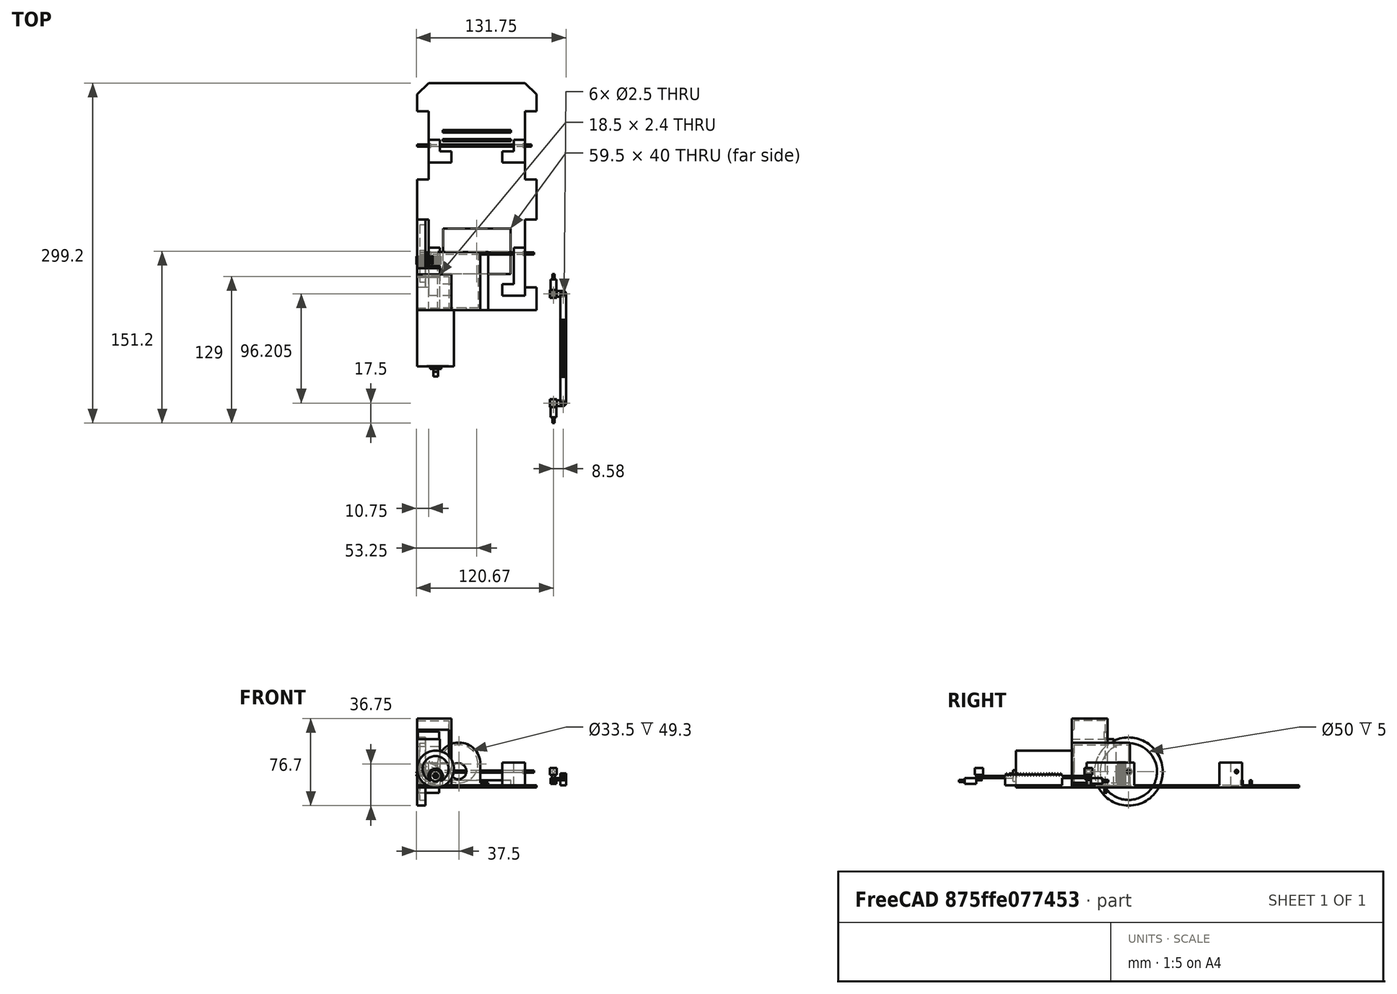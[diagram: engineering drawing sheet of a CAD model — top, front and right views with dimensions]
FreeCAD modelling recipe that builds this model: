
FCSTD DOCUMENT  (FreeCAD 0.21R33668 +26 (Git))
Label: spy_car_model
License: All rights reserved
LicenseURL: http://en.wikipedia.org/wiki/All_rights_reserved
objects: Sketcher::SketchObject×57, PartDesign::Pad×40, PartDesign::Pocket×18, PartDesign::Body×15, App::Part×9, PartDesign::Fillet×5, Part::Part2DObjectPython×3, Mesh::Feature×2, Spreadsheet::Sheet×1, PartDesign::FeaturePython×1
note: 202 computed .brp shape members not serialized (recipe doc carries the construction recipe); baked Part::Feature solids carry a one-line shape summary decoded from their .brp

FEATURE [Spreadsheet::Sheet] Spreadsheet
  cells = A1='12vdc gear motor; D1='servo ; G1='Car body; J1='rods; M1='motor holder; P1='turning mechanism; S1='wheels; A2='diameter; B2(dcm_diam)==32.5 mm; D2='total length; E2(serv_len)==45 mm; G2='height; H2(cb_height)==200 mm; J2='diameter; K2(rod_diam)==2 mm; M2='thickness; N2(mh_thick)==2 mm; P2='rack height; Q2(tm_rack_h)==7.25 mm; S2='back wheel diameter; T2(wheel_back_diam)==60 mm; A3='length; B3(dcm_len)==49.3 mm; D3='bottom to screw thing top; E3(serv_to_sec1)==31 mm; G3='width; H3(cb_width)==105 mm; J3='length; K3(rod_len)==100.5 mm; M3='dcm tolerance; N3(mh_tolerance)==1 mm; P3='rack thickness; Q3(tm_rack_thick)==5 mm; S3='back wheel thickness; T3(wheel_back_thick)==2.25 mm; A4='shaft_diamter; B4(dcm_shaft_diam)==4 mm; D4='bottom to first bump section; E4(serv_to_sec2)==37 mm; G4='thick ; H4(cb_thick)==2 mm; M4='dcm hole diameter; N4(mh_dcm_hole_diam)==B2 + N3; P4='distance from front ; Q4(tm_dist_from_front)==43.92 mm; S4='wheel hole diameter; T4(wheel_hole_diam)==K2; A5='shaft to flat side; B5(dcm_shaft_to_flat)==3 mm; D5='bottom to topbump section; E5(serv_to_sec3)==39 mm; G5='cb_flat_corners_adj_opp_len; H5(cb_flat_coprner_ao_len)==10 mm; M5='servo mount height bottom; N5(mh_servo_bottom_h)==10 mm; P5='height to bottom of tooth; Q5(tm_rack_height_to_bottom_tooth)==8.5 mm; S5='wheel hole walls thickness; T5(wheel_hole_wall_thick)==2 mm; A6='outer shaft bump diameter; B6(dcm_outer_shaft_bump)==10 mm; D6='width; E6(serv_w)==20 mm; G6='cb_flat_corner_len; H6(cb_flat_corner_len)==sqrt(H5 * H5 + H5 * H5); M6='servo mount height total; N6==E8; P6='rack length ; Q6(tm_rack_len)==50.27 mm; S6='wheel hole thing length; T6(wheel_holder_len)==4 mm; A7='motor inner indent ring diameter; B7(dcm_inner_indent)==21.9 mm; D7='height; E7(serv_h)==40.7 mm; G7='wheel space height; H7(cb_wheel_space_h)==60 mm; M7='holder screws thing height; N7(mh_screw_plat_h)==8 mm; P7='rack distance to edge; Q7==17.37 mm; S7='back wheel edge thickness; T7(wheel_back_edge_thick)==5 mm; A8='outer shaft bump outer ring dimater ; B8(dcm_outer_shaft_bump_outer_ring_diam)==14.2 mm; D8='length with screw things ; E8(serv_h_with_screws)==54 mm; G8='wheel space width; H8(cb_wheel_space_w)==10 mm; M8='motor distance right from origing; N8(mh_dcm_dist_from_origin)==52.5 mm; P8='rack arm thickness; Q8(tm_rack_arm_thick)==2 mm; S8='front wheel diameter; T8(wheel_front_diam)==(T2 / 2 - (H18 + H4) + 4.75 mm + K2 / 2) * 2; A9='shaft length; B9(dcm_shaft_len)==6.5 mm; D9='screw things height; E9(serv_screw_h)==(E8 - E7) / 2; G9='front wheel space from front distance; H9(cb_front_wheel_dist)==25 mm; M9='platform length; N9(mh_len)==B3 + N2; P9='rack arm length; Q9(tm_rack_arm_len)==25.46 mm; S9='front wheel thicknesss; T9(wheel_front_thick)==2.25 mm; A10='shaft flat area length ; B10(dcm_flat_area_len)==B9 * 0.6; D10='screw things thick; E10(serv_screw_thick)==2.4 mm; G10='back whee space from back distance; H10(cb_back_wheel_dist)==20 mm; M10='servo mount extra width; N10(mh_serv_extra_w)==30 mm - E6; P10='rack arm distance from origin; Q10(tm_rack_arm_odist)==1.25 mm; S10='front wheel edge thickness; T10(wheel_front_edge_thick)==5 mm; A11='outer shaft bump ring to bottom of dcm; B11(dcm_outer_shaft_bump_outer_ring_to_bottom)==17.4 mm; D11='screw holes diameter; E11(serv_screw_hole_diam)==4 mm; G11='gear hole width; H11(cb_gear_hole_w)==(H3 - 2 * H5) * 0.7; P11='rack screw diameter; Q11(tm_screw_diam)==2.5 mm; A12='indent depth; B12(dcm_inner_indent_depth)==0.5 mm; D12='screw things width; E12(serv_screw_w)==18.5 mm; G12='gear hole height; H12(cb_gear_hole_h)==40 mm; P12='rod turning piece width / height; Q12(tm_tp_wh)==6 mm; A13='shaft ouiter bump height; B13(dcm_outer_shaft_bump_height)==2.4 mm; D13='top edge to bottom of sec 3; E13(serv_sec_3_h)==34.1 mm; G13='gear hole from back distance; H13(cb_gear_hole_from_back)==H10 + H7 / 2 - H12 / 2; P13='rod turning piece length total; Q13(tm_tp_len)==7 mm; D14='section 3 thickness; E14(serv_sec_3_thick)==2 mm; G14='back wheeel axle holder height; H14(cb_axle_holder_h)==10 mm; P14='rod clearance ; Q14(tm_clearance)==7.75 mm; D15='smoothing factor; E15(serv_border_rad)==0.5 mm; G15='back wheel axle holder widht; H15(cb_axle_holder_thick)==10 mm; P15='rod turning piece rod length; Q15(tm_tp_rod_len)==5 mm; D16='servo shaft top bump diameter; E16(serv_shaft_bump_diam)==13 mm; G16='back wheel axle holder length; H16(cb_axle_holder_len)==20 mm; P16='rod turning piece length in rod; Q16(tm_tp_rod_in_len)==Q13 * 0.8; D17='servo shaft diameter; E17(serv_shaft_diam)==5.8 mm; G17='back wheel axle holder top width; H17(cb_axle_holder_top_thick)==10 mm; P17='rod turning piece length out rod; Q17(tm_tp_rod_out_len)==Q13 * 0.2; D18='servo shaft length; E18(serv_shaft_len)==5 mm; G18='axle hole height; H18(cb_axle_holder_hole_height)==H16 * 0.6; P18='rod tolerance; Q18(tm_tp_tolerance)==0.5 mm; D19='servo shaft top bump thick; E19(serv_shaft_bump_thick)==1 mm; G19='axle hole diameter; H19(cb_axle_hole_diameter)==K2 + 1 mm; P19='turning piece spinny axle length; Q19(tm_tp_spinny_rod_len)==4.75 mm; D20='servo shaft teeth count; E20(serv_shaft_teeth_num)=25; G20='gear hole offset; H20(cb_gear_hole_offset)==2 mm; P20='knuckle width; Q20(tm_knuckle_w)==5 mm; D21='shaft inner hole diamterer; E21(serv_shaft_hole_diam)==2.6 mm; G21='rack holder bump thick; H21(cb_rh_thick)==2 mm; P21='knuckle thickness; Q21(tm_knuckle_thick)==2 mm; D22='gear thickness; E22(serv_gear_thick)==7 mm; G22='rack holder height; H22(cb_rh_h)==Q5 / 2; P22='knuckle length; Q22(tm_knuckle_len)==10 mm; D23='gear diameter; E23(serv_gear_diam)==20 mm; G23='rack holder length; +31 more cells
FEATURE [Sketcher::SketchObject] Sketch  label="main car body sketch"
  FullyConstrained = true
  MapMode = 5
  Support = -> [XY_Plane]
  expr: Constraints[10] = Spreadsheet.cb_height
  expr: Constraints[12] = Spreadsheet.cb_width
  expr: Constraints[13] = Spreadsheet.cb_flat_coprner_ao_len
  expr: Constraints[14] = Spreadsheet.cb_flat_coprner_ao_len
  expr: Constraints[15] = Spreadsheet.cb_flat_coprner_ao_len
  sketch-geometry (6):
    g0: LineSegment StartX=-9e-16 StartY=0 StartZ=0 EndX=-9e-16 EndY=190 EndZ=0
    g1: LineSegment StartX=-9e-16 StartY=190 StartZ=0 EndX=10 EndY=200 EndZ=0
    g2: LineSegment StartX=10 StartY=200 StartZ=0 EndX=95 EndY=200 EndZ=0
    g3: LineSegment StartX=95 StartY=200 StartZ=0 EndX=105 EndY=190 EndZ=0
    g4: LineSegment StartX=105 StartY=190 StartZ=0 EndX=105 EndY=0 EndZ=0
    g5: LineSegment StartX=105 StartY=0 StartZ=0 EndX=0 EndY=0 EndZ=0
  constraints (17):
    c: Vertical(g0)
    c: Coincident(g1,g0)
    c: Coincident(g3,g2)
    c: Coincident(g4,g3)
    c: Vertical(g4)
    c: Coincident(g5,g4)
    c: Coincident(g0,g5)
    c: Horizontal(g5)
    c: Horizontal(g2)
    c: Coincident(g1,g2)
    c: DistanceY(g0,g1) = 200
    c: DistanceY(g3,g0) = 0
    c: DistanceX(g0,g4) = 105
    c: DistanceX(g0,g1) = 10
    c: DistanceX(g2,g3) = 10
    c: DistanceY(g0,g1) = 10
    c: Coincident(g-1,g0)
FEATURE [PartDesign::Pad] Pad
  Direction = (0,0,1)
  Length = 2
  Length2 = 10
  Profile = -> Sketch
  ReferenceAxis = -> Sketch [N_Axis]
  Type = 0
  expr: Length = Spreadsheet.cb_thick
FEATURE [Sketcher::SketchObject] Sketch001
  FullyConstrained = true
  MapMode = 5
  Placement = pos=(0,0,0) rot=(1,0,0;1.5708rad)
  Support = -> [XZ_Plane003]
  expr: Constraints[0] = Spreadsheet.dcm_diam
  expr: Constraints[1] = Spreadsheet.dcm_diam / 2
  expr: Constraints[2] = Spreadsheet.dcm_diam / 2
  sketch-geometry (1):
    g0: Circle CenterX=16.25 CenterY=16.25 CenterZ=0 NormalX=0 NormalY=0 NormalZ=1 AngleXU=0 Radius=16.25
  constraints (3):
    c: Diameter(g0) = 32.5
    c: DistanceX(g-1,g0) = 16.25
    c: DistanceY(g-1,g0) = 16.25
FEATURE [PartDesign::Pad] Pad001
  Direction = (0,-1,-2e-16)
  Length = 49.3
  Length2 = 10
  Placement = pos=(0,0,0) rot=(1,0,0;1.5708rad)
  Profile = -> Sketch001
  ReferenceAxis = -> Sketch001 [N_Axis]
  Type = 0
  expr: Length = Spreadsheet.dcm_len
FEATURE [Sketcher::SketchObject] Sketch002
  FullyConstrained = false
  MapMode = 5
  Placement = pos=(0,-49.3,-1.09e-14) rot=(1,0,0;1.5708rad)
  Support = -> [Pad001]
  expr: Constraints[0] = Spreadsheet.dcm_diam / 2
  expr: Constraints[1] = Spreadsheet.dcm_diam / 2
  sketch-geometry (1):
    g0: Circle CenterX=16.25 CenterY=16.25 CenterZ=0 NormalX=0 NormalY=0 NormalZ=1 AngleXU=0 Radius=11.409
  constraints (2):
    c: DistanceX(g-1,g0) = 16.25
    c: DistanceY(g-1,g0) = 16.25
FEATURE [PartDesign::Pocket] Pocket
  BaseFeature = -> Pad001
  Direction = (0,1,2e-16)
  Length = 0.5
  Length2 = 5
  Placement = pos=(0,0,0) rot=(1,0,0;1.5708rad)
  Profile = -> Sketch002
  ReferenceAxis = -> Sketch002 [N_Axis]
  Type = 0
  expr: Length = Spreadsheet.dcm_inner_indent_depth
FEATURE [Sketcher::SketchObject] Sketch003
  FullyConstrained = false
  MapMode = 5
  Placement = pos=(-1.01e-14,-48.8,-1.75e-14) rot=(1,0,0;1.5708rad)
  Support = -> [Pocket]
  expr: Constraints[0] = Spreadsheet.dcm_diam / 2
  expr: Constraints[1] = Spreadsheet.dcm_outer_shaft_bump_outer_ring_to_bottom - Spreadsheet.dcm_outer_shaft_bump_outer_ring_diam / 2
  sketch-geometry (1):
    g0: Circle CenterX=16.25 CenterY=10.3 CenterZ=0 NormalX=0 NormalY=0 NormalZ=1 AngleXU=0 Radius=6.29816
  constraints (2):
    c: DistanceX(g-1,g0) = 16.25
    c: DistanceY(g-1,g0) = 10.3
FEATURE [PartDesign::Pad] Pad002
  BaseFeature = -> Pocket
  Direction = (-2e-16,-1,-2e-16)
  Length = 0.5
  Length2 = 10
  Placement = pos=(0,0,0) rot=(1,0,0;1.5708rad)
  Profile = -> Sketch003
  ReferenceAxis = -> Sketch003 [N_Axis]
  Type = 0
  expr: Length = Spreadsheet.dcm_inner_indent_depth
FEATURE [Sketcher::SketchObject] Sketch004
  FullyConstrained = true
  MapMode = 5
  Placement = pos=(0,-49.3,0) rot=(1,0,0;1.5708rad)
  Support = -> [Pad002]
  expr: Constraints[0] = Spreadsheet.dcm_diam / 2
  expr: Constraints[1] = Spreadsheet.dcm_outer_shaft_bump
  expr: Constraints[2] = Spreadsheet.dcm_outer_shaft_bump_outer_ring_to_bottom - Spreadsheet.dcm_outer_shaft_bump_outer_ring_diam / 2
  sketch-geometry (1):
    g0: Circle CenterX=16.25 CenterY=10.3 CenterZ=0 NormalX=0 NormalY=0 NormalZ=1 AngleXU=0 Radius=5
  constraints (3):
    c: DistanceX(g-1,g0) = 16.25
    c: Diameter(g0) = 10
    c: DistanceY(g-1,g0) = 10.3
FEATURE [PartDesign::Pad] Pad003
  BaseFeature = -> Pad002
  Direction = (0,-1,2e-16)
  Length = 2.4
  Length2 = 10
  Placement = pos=(0,0,0) rot=(1,0,0;1.5708rad)
  Profile = -> Sketch004
  ReferenceAxis = -> Sketch004 [N_Axis]
  Type = 0
  expr: Length = Spreadsheet.dcm_outer_shaft_bump_height
FEATURE [Sketcher::SketchObject] Sketch005
  FullyConstrained = true
  MapMode = 5
  Placement = pos=(0,-51.7,0) rot=(1,0,0;1.5708rad)
  Support = -> [Pad003]
  expr: Constraints[0] = Spreadsheet.dcm_diam / 2
  expr: Constraints[1] = Spreadsheet.dcm_outer_shaft_bump_outer_ring_to_bottom - Spreadsheet.dcm_outer_shaft_bump_outer_ring_diam / 2
  expr: Constraints[2] = Spreadsheet.dcm_shaft_diam
  sketch-geometry (1):
    g0: Circle CenterX=16.25 CenterY=10.3 CenterZ=0 NormalX=0 NormalY=0 NormalZ=1 AngleXU=0 Radius=2
  constraints (3):
    c: DistanceX(g-1,g0) = 16.25
    c: DistanceY(g-1,g0) = 10.3
    c: Diameter(g0) = 4
FEATURE [PartDesign::Pad] Pad004
  BaseFeature = -> Pad003
  Direction = (0,-1,2e-16)
  Length = 2.6
  Length2 = 10
  Placement = pos=(0,0,0) rot=(1,0,0;1.5708rad)
  Profile = -> Sketch005
  ReferenceAxis = -> Sketch005 [N_Axis]
  Type = 0
  expr: Length = Spreadsheet.dcm_shaft_len - Spreadsheet.dcm_flat_area_len
FEATURE [Sketcher::SketchObject] Sketch006
  FullyConstrained = true
  MapMode = 5
  Placement = pos=(0,-54.3,0) rot=(1,0,0;1.5708rad)
  Support = -> [Pad004]
  expr: Constraints[0] = Spreadsheet.dcm_diam / 2
  expr: Constraints[1] = Spreadsheet.dcm_shaft_diam
  expr: Constraints[2] = Spreadsheet.dcm_outer_shaft_bump_outer_ring_to_bottom - Spreadsheet.dcm_outer_shaft_bump_outer_ring_diam / 2
  sketch-geometry (2):
    g0: ArcOfCircle CenterX=16.25 CenterY=10.3 CenterZ=0 NormalX=0 NormalY=0 NormalZ=1 AngleXU=0 Radius=2 StartAngle=3.14159 EndAngle=6.28319
    g1: LineSegment StartX=14.25 StartY=10.3 StartZ=0 EndX=18.25 EndY=10.3 EndZ=0
  constraints (7):
    c: DistanceX(g-1,g0) = 16.25
    c: Diameter(g0) = 4
    c: DistanceY(g-1,g0) = 10.3
    c: DistanceY(g0,g0) = 0
    c: DistanceY(g0,g0) = 0
    c: Coincident(g1,g0)
    c: Coincident(g1,g0)
FEATURE [PartDesign::Pad] Pad005
  BaseFeature = -> Pad004
  Direction = (0,-1,2e-16)
  Length = 3.9
  Length2 = 10
  Placement = pos=(0,0,0) rot=(1,0,0;1.5708rad)
  Profile = -> Sketch006
  ReferenceAxis = -> Sketch006 [N_Axis]
  Type = 0
  expr: Length = Spreadsheet.dcm_flat_area_len
FEATURE [PartDesign::Body] Body001  label="motor_body"
  Group = -> [Sketch001,Pad001,Sketch002,Pocket,Sketch003,Pad002,Sketch004,Pad003,Sketch005,Pad004,Sketch006,Pad005]
  Origin = -> Origin003
  Tip = -> Pad005
FEATURE [Sketcher::SketchObject] Sketch007  label="car body holes sketch"
  FullyConstrained = false
  MapMode = 5
  Placement = pos=(0,0,2) rot=(0,0,1;0rad)
  Support = -> [Pad]
  expr: Constraints[18] = Spreadsheet.cb_wheel_space_w
  expr: Constraints[19] = Spreadsheet.cb_wheel_space_h
  expr: Constraints[28] = Spreadsheet.cb_wheel_space_w
  expr: Constraints[29] = Spreadsheet.cb_wheel_space_h
  expr: Constraints[38] = Spreadsheet.cb_wheel_space_w
  expr: Constraints[39] = Spreadsheet.cb_wheel_space_h
  expr: Constraints[43] = Spreadsheet.cb_back_wheel_dist
  expr: Constraints[44] = Spreadsheet.cb_height - Spreadsheet.cb_front_wheel_dist
  expr: Constraints[47] = Spreadsheet.cb_width
  expr: Constraints[48] = Spreadsheet.cb_width
  expr: Constraints[57] = Spreadsheet.cb_gear_hole_from_back + Spreadsheet.cb_gear_hole_offset
  expr: Constraints[58] = Spreadsheet.cb_gear_hole_h
  expr: Constraints[59] = Spreadsheet.cb_gear_hole_w
  expr: Constraints[60] = Spreadsheet.cb_width / 2 - Spreadsheet.cb_gear_hole_w / 2
  expr: Constraints[8] = Spreadsheet.cb_wheel_space_w
  expr: Constraints[9] = Spreadsheet.cb_wheel_space_h
  sketch-geometry (21):
    g0: LineSegment StartX=0 StartY=80 StartZ=0 EndX=10 EndY=80 EndZ=0
    g1: LineSegment StartX=10 StartY=80 StartZ=0 EndX=10 EndY=20 EndZ=0
    g2: LineSegment StartX=10 StartY=20 StartZ=0 EndX=0 EndY=20 EndZ=0
    g3: LineSegment StartX=0 StartY=20 StartZ=0 EndX=0 EndY=80 EndZ=0
    g4: LineSegment StartX=95 StartY=80 StartZ=0 EndX=105 EndY=80 EndZ=0
    g5: LineSegment StartX=105 StartY=80 StartZ=0 EndX=105 EndY=20 EndZ=0
    g6: LineSegment StartX=105 StartY=20 StartZ=0 EndX=95 EndY=20 EndZ=0
    g7: LineSegment StartX=95 StartY=20 StartZ=0 EndX=95 EndY=80 EndZ=0
    g8: LineSegment StartX=0 StartY=175 StartZ=0 EndX=10 EndY=175 EndZ=0
    g9: LineSegment StartX=10 StartY=175 StartZ=0 EndX=10 EndY=115 EndZ=0
    g10: LineSegment StartX=10 StartY=115 StartZ=0 EndX=0 EndY=115 EndZ=0
    g11: LineSegment StartX=0 StartY=115 StartZ=0 EndX=0 EndY=175 EndZ=0
    g12: LineSegment StartX=95 StartY=175 StartZ=0 EndX=105 EndY=175 EndZ=0
    g13: LineSegment StartX=105 StartY=175 StartZ=0 EndX=105 EndY=115 EndZ=0
    g14: LineSegment StartX=105 StartY=115 StartZ=0 EndX=95 EndY=115 EndZ=0
    g15: LineSegment StartX=95 StartY=115 StartZ=0 EndX=95 EndY=175 EndZ=0
    g16: GeomPoint X=0 Y=200 Z=0
    g17: LineSegment StartX=22.75 StartY=72 StartZ=0 EndX=82.25 EndY=72 EndZ=0
    g18: LineSegment StartX=82.25 StartY=72 StartZ=0 EndX=82.25 EndY=32 EndZ=0
    g19: LineSegment StartX=82.25 StartY=32 StartZ=0 EndX=22.75 EndY=32 EndZ=0
    g20: LineSegment StartX=22.75 StartY=32 StartZ=0 EndX=22.75 EndY=72 EndZ=0
  constraints (61):
    c: Coincident(g0,g1)
    c: Coincident(g1,g2)
    c: Coincident(g2,g3)
    c: Coincident(g3,g0)
    c: Horizontal(g0)
    c: Horizontal(g2)
    c: Vertical(g1)
    c: Vertical(g3)
    c: DistanceX(g0,g0) = 10
    c: DistanceY(g2,g0) = 60
    c: Coincident(g4,g5)
    c: Coincident(g5,g6)
    c: Coincident(g6,g7)
    c: Coincident(g7,g4)
    c: Horizontal(g4)
    c: Horizontal(g6)
    c: Vertical(g5)
    c: Vertical(g7)
    c: DistanceX(g4,g4) = 10
    c: DistanceY(g6,g4) = 60
    c: Coincident(g8,g9)
    c: Coincident(g9,g10)
    c: Coincident(g10,g11)
    c: Coincident(g11,g8)
    c: Horizontal(g8)
    c: Horizontal(g10)
    c: Vertical(g9)
    c: Vertical(g11)
    c: DistanceX(g8,g8) = 10
    c: DistanceY(g10,g8) = 60
    c: Coincident(g12,g13)
    c: Coincident(g13,g14)
    c: Coincident(g14,g15)
    c: Coincident(g15,g12)
    c: Horizontal(g12)
    c: Horizontal(g14)
    c: Vertical(g13)
    c: Vertical(g15)
    c: DistanceX(g12,g12) = 10
    c: DistanceY(g14,g12) = 60
    c: DistanceX(g-1,g2) = 0
    c: DistanceX(g-1,g10) = 0
    c: PointOnObject(g16,g-2)
    c: DistanceY(g-1,g2) = 20
    c: DistanceY(g-1,g8) = 175
    c: DistanceY(g9,g14) = 0
    c: DistanceY(g6,g1) = 0
    c: DistanceX(g-1,g5) = 105
    c: DistanceX(g-1,g13) = 105
    c: Coincident(g17,g18)
    c: Coincident(g18,g19)
    c: Coincident(g19,g20)
    c: Coincident(g20,g17)
    c: Horizontal(g17)
    c: Horizontal(g19)
    c: Vertical(g18)
    c: Vertical(g20)
    c: DistanceY(g-1,g19) = 32
    c: DistanceY(g19,g17) = 40
    c: DistanceX(g17,g17) = 59.5
    c: DistanceX(g-1,g19) = 22.75
FEATURE [Mesh::Feature] dcm_bevel_gear
  Placement = pos=(16,-55,10) rot=(1,0,0;1.5708rad)
FEATURE [App::Part] Part001  label="12vdc_gear_motor"
  Group = -> [Body001,dcm_bevel_gear]
  Origin = -> Origin002
  Placement = pos=(20.5,123.3,4.5) rot=(0,1,0;0rad)
  expr: .Placement.Base.x = Spreadsheet.cb_width / 2 - Spreadsheet.dcm_diam + Spreadsheet.mh_tolerance / 2 + 0 mm
  expr: .Placement.Base.y = Spreadsheet.cb_back_wheel_dist + Spreadsheet.dcm_len + Spreadsheet.cb_wheel_space_h - 6 mm
  expr: .Placement.Base.z = Spreadsheet.cb_thick + Spreadsheet.mh_thick + Spreadsheet.mh_tolerance / 2
FEATURE [PartDesign::Pocket] Pocket001  label="car holes"
  BaseFeature = -> Pad
  Direction = (0,0,-1)
  Length = 2
  Length2 = 5
  Profile = -> Sketch007
  ReferenceAxis = -> Sketch007 [N_Axis]
  Type = 0
  expr: Length = Spreadsheet.cb_thick
FEATURE [Sketcher::SketchObject] Sketch015  label="right axle holder hole sketch"
  AttachmentOffset = pos=(0,0,95) rot=(0,0,1;0rad)
  FullyConstrained = true
  MapMode = 5
  Placement = pos=(95,-2.11e-14,2.11e-14) rot=(0.57735,0.57735,0.57735;2.0944rad)
  Support = -> [YZ_Plane]
  expr: .AttachmentOffset.Base.z = Spreadsheet.cb_width - Spreadsheet.cb_wheel_space_w
  expr: Constraints[0] = Spreadsheet.cb_axle_hole_diameter
  expr: Constraints[1] = Spreadsheet.cb_back_wheel_dist + Spreadsheet.cb_wheel_space_h / 2
  expr: Constraints[2] = Spreadsheet.cb_thick + Spreadsheet.cb_axle_holder_hole_height
  sketch-geometry (1):
    g0: Circle CenterX=50 CenterY=14 CenterZ=0 NormalX=0 NormalY=0 NormalZ=1 AngleXU=0 Radius=1.5
  constraints (3):
    c: Diameter(g0) = 3
    c: DistanceX(g-1,g0) = 50
    c: DistanceY(g-1,g0) = 14
FEATURE [Sketcher::SketchObject] Sketch014  label="left axle holder hole sketch"
  AttachmentOffset = pos=(0,0,10) rot=(0,0,1;0rad)
  FullyConstrained = true
  MapMode = 5
  Placement = pos=(10,-2.2e-15,2.2e-15) rot=(0.57735,0.57735,0.57735;2.0944rad)
  Support = -> [YZ_Plane]
  expr: .AttachmentOffset.Base.z = Spreadsheet.cb_wheel_space_w
  expr: Constraints[0] = Spreadsheet.cb_back_wheel_dist + Spreadsheet.cb_wheel_space_h / 2
  expr: Constraints[1] = Spreadsheet.cb_thick + Spreadsheet.cb_axle_holder_hole_height
  expr: Constraints[2] = Spreadsheet.cb_axle_hole_diameter
  sketch-geometry (1):
    g0: Circle CenterX=50 CenterY=14 CenterZ=0 NormalX=0 NormalY=0 NormalZ=1 AngleXU=0 Radius=1.5
  constraints (3):
    c: DistanceX(g-1,g0) = 50
    c: DistanceY(g-1,g0) = 14
    c: Diameter(g0) = 3
FEATURE [Sketcher::SketchObject] Sketch016  label="back axle holder sketch"
  AttachmentOffset = pos=(0,0,-45) rot=(0,0,1;0rad)
  FullyConstrained = true
  MapMode = 5
  Placement = pos=(0,45,1e-14) rot=(1,0,0;1.5708rad)
  Support = -> [XZ_Plane]
  expr: .AttachmentOffset.Base.z = -Spreadsheet.cb_back_wheel_dist - Spreadsheet.cb_wheel_space_h / 2 + Spreadsheet.cb_axle_holder_h / 2
  expr: Constraints[11] = Spreadsheet.cb_axle_holder_len
  expr: Constraints[19] = Spreadsheet.cb_axle_holder_top_thick
  expr: Constraints[20] = Spreadsheet.cb_axle_holder_thick
  expr: Constraints[21] = Spreadsheet.cb_axle_holder_len
  expr: Constraints[22] = Spreadsheet.cb_width - Spreadsheet.cb_wheel_space_w
  expr: Constraints[23] = Spreadsheet.cb_thick
  expr: Constraints[5] = Spreadsheet.cb_axle_holder_thick
  expr: Constraints[6] = Spreadsheet.cb_axle_holder_top_thick
  expr: Constraints[7] = Spreadsheet.cb_thick
  expr: Constraints[8] = Spreadsheet.cb_wheel_space_w
  sketch-geometry (8):
    g0: LineSegment StartX=10 StartY=2 StartZ=0 EndX=20 EndY=2 EndZ=0
    g1: LineSegment StartX=10 StartY=22 StartZ=0 EndX=20 EndY=22 EndZ=0
    g2: LineSegment StartX=10 StartY=22 StartZ=0 EndX=10 EndY=2 EndZ=0
    g3: LineSegment StartX=20 StartY=22 StartZ=0 EndX=20 EndY=2 EndZ=0
    g4: LineSegment StartX=85 StartY=22 StartZ=0 EndX=85 EndY=2 EndZ=0
    g5: LineSegment StartX=85 StartY=22 StartZ=0 EndX=95 EndY=22 EndZ=0
    g6: LineSegment StartX=95 StartY=22 StartZ=0 EndX=95 EndY=2 EndZ=0
    g7: LineSegment StartX=95 StartY=2 StartZ=0 EndX=85 EndY=2 EndZ=0
  constraints (24):
    c: Horizontal(g0)
    c: Horizontal(g1)
    c: Coincident(g2,g1)
    c: Coincident(g2,g0)
    c: Vertical(g2)
    c: DistanceX(g0,g0) = 10
    c: DistanceX(g1,g1) = 10
    c: DistanceY(g-1,g0) = 2
    c: DistanceX(g-1,g0) = 10
    c: Coincident(g3,g1)
    c: Coincident(g3,g0)
    c: DistanceY(g0,g1) = 20
    c: Coincident(g5,g4)
    c: Horizontal(g5)
    c: Coincident(g6,g5)
    c: Vertical(g6)
    c: Coincident(g7,g6)
    c: Coincident(g7,g4)
    c: Horizontal(g7)
    c: DistanceX(g4,g5) = 10
    c: DistanceX(g4,g6) = 10
    c: DistanceY(g6,g5) = 20
    c: DistanceX(g-1,g6) = 95
    c: DistanceY(g-1,g4) = 2
FEATURE [PartDesign::Pad] Pad006
  BaseFeature = -> Pocket001
  Direction = (0,-1,-2e-16)
  Length = 10
  Length2 = 10
  Profile = -> Sketch016
  ReferenceAxis = -> Sketch016 [N_Axis]
  Reversed = true
  Type = 0
  expr: Length = Spreadsheet.cb_axle_holder_h
FEATURE [PartDesign::Pocket] Pocket002
  BaseFeature = -> Pad006
  Direction = (-1,2e-16,-3e-16)
  Length = 2
  Length2 = 5
  Profile = -> Sketch014
  ReferenceAxis = -> Sketch014 [N_Axis]
  Reversed = true
  Type = 0
  expr: Length = Spreadsheet.cb_axle_holder_thick * 0.2
FEATURE [PartDesign::Pocket] Pocket003
  BaseFeature = -> Pocket002
  Direction = (-1,2e-16,-3e-16)
  Length = 2
  Length2 = 5
  Profile = -> Sketch015
  ReferenceAxis = -> Sketch015 [N_Axis]
  Type = 0
  expr: Length = Spreadsheet.cb_axle_holder_thick * 0.2
FEATURE [Mesh::Feature] shaft_bevel_gear
  Placement = pos=(24,50,14) rot=(0,1,0;1.5708rad)
  expr: .Placement.Base.y = Spreadsheet.cb_back_wheel_dist + Spreadsheet.cb_wheel_space_h / 2
  expr: .Placement.Base.z = Spreadsheet.cb_thick + Spreadsheet.cb_axle_holder_hole_height
FEATURE [Sketcher::SketchObject] Sketch017
  FullyConstrained = true
  MapMode = 5
  Placement = pos=(0,0,0) rot=(0.57735,0.57735,0.57735;2.0944rad)
  Support = -> [YZ_Plane005]
  expr: Constraints[0] = Spreadsheet.rod_diam
  expr: Constraints[1] = Spreadsheet.cb_back_wheel_dist + Spreadsheet.cb_wheel_space_h / 2
  expr: Constraints[2] = Spreadsheet.cb_thick + Spreadsheet.cb_axle_holder_hole_height
  sketch-geometry (1):
    g0: Circle CenterX=50 CenterY=14 CenterZ=0 NormalX=0 NormalY=0 NormalZ=1 AngleXU=0 Radius=1
  constraints (3):
    c: Diameter(g0) = 2
    c: DistanceX(g-1,g0) = 50
    c: DistanceY(g-1,g0) = 14
FEATURE [PartDesign::Pad] Pad007
  Direction = (1,-2e-16,3e-16)
  Length = 100.5
  Length2 = 10
  Placement = pos=(0,0,0) rot=(1,1,1;2.0944rad)
  Profile = -> Sketch017
  ReferenceAxis = -> Sketch017 [N_Axis]
  Type = 0
  expr: Length = Spreadsheet.rod_len
FEATURE [PartDesign::Body] Body002  label="rod"
  Group = -> [Sketch017,Pad007]
  Origin = -> Origin005
  Placement = pos=(2.25,0,0) rot=(0,0,1;0rad)
  Tip = -> Pad007
  expr: .Placement.Base.x = (Spreadsheet.cb_width - Spreadsheet.rod_len) / 2
FEATURE [App::Part] Part002  label="back rod"
  Group = -> [Body002,shaft_bevel_gear]
  Origin = -> Origin004
FEATURE [Sketcher::SketchObject] Sketch018
  FullyConstrained = true
  MapMode = 5
  Placement = pos=(0,0,0) rot=(1,0,0;1.5708rad)
  Support = -> [XZ_Plane007]
  expr: Constraints[10] = Spreadsheet.mh_dcm_dist_from_origin - Spreadsheet.dcm_diam - Spreadsheet.mh_screw_plat_h - Spreadsheet.mh_thick
  expr: Constraints[11] = Spreadsheet.cb_thick
  expr: Constraints[8] = Spreadsheet.mh_thick
  expr: Constraints[9] = Spreadsheet.mh_screw_plat_h * 2 + Spreadsheet.dcm_diam + Spreadsheet.mh_thick * 2
  sketch-geometry (4):
    g0: LineSegment StartX=10 StartY=4 StartZ=0 EndX=62.5 EndY=4 EndZ=0
    g1: LineSegment StartX=62.5 StartY=4 StartZ=0 EndX=62.5 EndY=2 EndZ=0
    g2: LineSegment StartX=62.5 StartY=2 StartZ=0 EndX=10 EndY=2 EndZ=0
    g3: LineSegment StartX=10 StartY=2 StartZ=0 EndX=10 EndY=4 EndZ=0
  constraints (12):
    c: Coincident(g0,g1)
    c: Coincident(g1,g2)
    c: Coincident(g2,g3)
    c: Coincident(g3,g0)
    c: Horizontal(g0)
    c: Horizontal(g2)
    c: Vertical(g1)
    c: Vertical(g3)
    c: DistanceY(g1,g0) = 2
    c: DistanceX(g0,g0) = 52.5
    c: DistanceX(g-1,g2) = 10
    c: DistanceY(g-1,g2) = 2
FEATURE [Sketcher::SketchObject] Sketch020
  FullyConstrained = true
  MapMode = 5
  Placement = pos=(0,0,0) rot=(1,0,0;1.5708rad)
  Support = -> [XZ_Plane009]
  expr: Constraints[10] = Spreadsheet.cb_thick
  expr: Constraints[8] = Spreadsheet.serv_w
  expr: Constraints[9] = Spreadsheet.serv_h
  sketch-geometry (4):
    g0: LineSegment StartX=0 StartY=42.7 StartZ=0 EndX=20 EndY=42.7 EndZ=0
    g1: LineSegment StartX=20 StartY=42.7 StartZ=0 EndX=20 EndY=2 EndZ=0
    g2: LineSegment StartX=20 StartY=2 StartZ=0 EndX=0 EndY=2 EndZ=0
    g3: LineSegment StartX=0 StartY=2 StartZ=0 EndX=0 EndY=42.7 EndZ=0
  constraints (12):
    c: Coincident(g0,g1)
    c: Coincident(g1,g2)
    c: Coincident(g2,g3)
    c: Coincident(g3,g0)
    c: Horizontal(g0)
    c: Horizontal(g2)
    c: Vertical(g1)
    c: Vertical(g3)
    c: DistanceX(g0,g0) = 20
    c: DistanceY(g2,g0) = 40.7
    c: DistanceY(g-1,g2) = 2
    c: DistanceX(g-1,g2) = 0
FEATURE [PartDesign::Pad] Pad008
  Direction = (0,-1,-2e-16)
  Length = 37
  Length2 = 10
  Placement = pos=(0,0,0) rot=(1,0,0;1.5708rad)
  Profile = -> Sketch020
  ReferenceAxis = -> Sketch020 [N_Axis]
  Reversed = true
  Type = 0
  expr: Length = Spreadsheet.serv_to_sec2
FEATURE [Sketcher::SketchObject] Sketch021
  FullyConstrained = true
  MapMode = 5
  Placement = pos=(0,-9.5e-15,42.7) rot=(0,0,1;3.14159rad)
  Support = -> [Pad008]
  expr: Constraints[10] = Spreadsheet.serv_to_sec1
  expr: Constraints[11] = Spreadsheet.serv_w / 2 - Spreadsheet.serv_screw_w / 2
  expr: Constraints[8] = Spreadsheet.serv_screw_thick
  expr: Constraints[9] = Spreadsheet.serv_screw_w
  sketch-geometry (4):
    g0: LineSegment StartX=-19.25 StartY=-28.6 StartZ=0 EndX=-0.75 EndY=-28.6 EndZ=0
    g1: LineSegment StartX=-0.75 StartY=-28.6 StartZ=0 EndX=-0.75 EndY=-31 EndZ=0
    g2: LineSegment StartX=-0.75 StartY=-31 StartZ=0 EndX=-19.25 EndY=-31 EndZ=0
    g3: LineSegment StartX=-19.25 StartY=-31 StartZ=0 EndX=-19.25 EndY=-28.6 EndZ=0
  constraints (12):
    c: Coincident(g0,g1)
    c: Coincident(g1,g2)
    c: Coincident(g2,g3)
    c: Coincident(g3,g0)
    c: Horizontal(g0)
    c: Horizontal(g2)
    c: Vertical(g1)
    c: Vertical(g3)
    c: DistanceY(g1,g0) = 2.4
    c: DistanceX(g0,g0) = 18.5
    c: DistanceY(g1,g-1) = 31
    c: DistanceX(g1,g-1) = 0.75
FEATURE [Sketcher::SketchObject] Sketch022
  FullyConstrained = true
  MapMode = 5
  Placement = pos=(0,-4e-16,2) rot=(1,0,0;3.14159rad)
  Support = -> [Pad008]
  expr: Constraints[10] = Spreadsheet.serv_to_sec1
  expr: Constraints[11] = Spreadsheet.serv_w / 2 - Spreadsheet.serv_screw_w / 2
  expr: Constraints[8] = Spreadsheet.serv_screw_thick
  expr: Constraints[9] = Spreadsheet.serv_screw_w
  sketch-geometry (4):
    g0: LineSegment StartX=0.75 StartY=-28.6 StartZ=0 EndX=19.25 EndY=-28.6 EndZ=0
    g1: LineSegment StartX=19.25 StartY=-28.6 StartZ=0 EndX=19.25 EndY=-31 EndZ=0
    g2: LineSegment StartX=19.25 StartY=-31 StartZ=0 EndX=0.75 EndY=-31 EndZ=0
    g3: LineSegment StartX=0.75 StartY=-31 StartZ=0 EndX=0.75 EndY=-28.6 EndZ=0
  constraints (12):
    c: Coincident(g0,g1)
    c: Coincident(g1,g2)
    c: Coincident(g2,g3)
    c: Coincident(g3,g0)
    c: Horizontal(g0)
    c: Horizontal(g2)
    c: Vertical(g1)
    c: Vertical(g3)
    c: DistanceY(g2,g0) = 2.4
    c: DistanceX(g0,g0) = 18.5
    c: DistanceY(g2,g-1) = 31
    c: DistanceX(g-1,g2) = 0.75
FEATURE [PartDesign::Pad] Pad009
  BaseFeature = -> Pad008
  Direction = (0,-2e-16,1)
  Length = 6.65
  Length2 = 10
  Placement = pos=(0,0,0) rot=(1,0,0;1.5708rad)
  Profile = -> Sketch021
  ReferenceAxis = -> Sketch021 [N_Axis]
  Type = 0
  expr: Length = Spreadsheet.serv_screw_h
FEATURE [PartDesign::Pad] Pad010
  BaseFeature = -> Pad009
  Direction = (0,2e-16,-1)
  Length = 6.65
  Length2 = 10
  Placement = pos=(0,0,0) rot=(1,0,0;1.5708rad)
  Profile = -> Sketch022
  ReferenceAxis = -> Sketch022 [N_Axis]
  Type = 0
  expr: Length = Spreadsheet.serv_screw_h
FEATURE [Sketcher::SketchObject] Sketch023
  FullyConstrained = true
  MapMode = 5
  Placement = pos=(0,37,8.2e-15) rot=(-1,0,0;1.5708rad)
  Support = -> [Pad010]
  expr: Constraints[10] = Spreadsheet.serv_w
  expr: Constraints[12] = Spreadsheet.serv_w / 2
  expr: Constraints[1] = Spreadsheet.serv_w / 2 + Spreadsheet.cb_thick
  expr: Constraints[9] = Spreadsheet.serv_sec_3_h + Spreadsheet.cb_thick
  sketch-geometry (4):
    g0: ArcOfCircle CenterX=10 CenterY=-12 CenterZ=0 NormalX=0 NormalY=0 NormalZ=1 AngleXU=0 Radius=10 StartAngle=0 EndAngle=3.14159
    g1: LineSegment StartX=0 StartY=-12 StartZ=0 EndX=0 EndY=-36.1 EndZ=0
    g2: LineSegment StartX=0 StartY=-36.1 StartZ=0 EndX=20 EndY=-36.1 EndZ=0
    g3: LineSegment StartX=20 StartY=-12 StartZ=0 EndX=20 EndY=-36.1 EndZ=0
  constraints (13):
    c: DistanceY(g0,g0) = 0
    c: DistanceY(g0,g-1) = 12
    c: Coincident(g1,g0)
    c: PointOnObject(g1,g-2)
    c: Coincident(g2,g1)
    c: Horizontal(g2)
    c: Coincident(g3,g0)
    c: Coincident(g3,g2)
    c: Vertical(g3)
    c: DistanceY(g1,g-1) = 36.1
    c: Diameter(g0) = 20
    c: DistanceY(g0,g0) = 0
    c: DistanceX(g-1,g0) = 10
FEATURE [PartDesign::Pad] Pad011
  BaseFeature = -> Pad010
  Direction = (0,1,2e-16)
  Length = 2
  Length2 = 10
  Placement = pos=(0,0,0) rot=(1,0,0;1.5708rad)
  Profile = -> Sketch023
  ReferenceAxis = -> Sketch023 [N_Axis]
  Type = 0
  expr: Length = Spreadsheet.serv_sec_3_thick
FEATURE [PartDesign::Fillet] Fillet
  Base = -> Pad011 [Edge3]
  BaseFeature = -> Pad011
  Placement = pos=(0,0,0) rot=(1,0,0;1.5708rad)
  Radius = 0.5
  SupportTransform = false
  UseAllEdges = false
  expr: Radius = Spreadsheet.serv_border_rad
FEATURE [Sketcher::SketchObject] Sketch024
  FullyConstrained = true
  MapMode = 5
  Placement = pos=(0,39,9.6e-15) rot=(-1,0,0;1.5708rad)
  Support = -> [Fillet]
  expr: Constraints[0] = Spreadsheet.serv_w / 2
  expr: Constraints[1] = Spreadsheet.serv_w / 2 + Spreadsheet.cb_thick
  expr: Constraints[2] = Spreadsheet.serv_shaft_bump_diam
  sketch-geometry (1):
    g0: Circle CenterX=10 CenterY=-12 CenterZ=0 NormalX=0 NormalY=0 NormalZ=1 AngleXU=0 Radius=6.5
  constraints (3):
    c: DistanceX(g-1,g0) = 10
    c: DistanceY(g0,g-1) = 12
    c: Diameter(g0) = 13
FEATURE [PartDesign::Pad] Pad012
  BaseFeature = -> Fillet
  Direction = (0,1,2e-16)
  Length = 1
  Length2 = 10
  Placement = pos=(0,0,0) rot=(1,0,0;1.5708rad)
  Profile = -> Sketch024
  ReferenceAxis = -> Sketch024 [N_Axis]
  Type = 0
  expr: Length = Spreadsheet.serv_shaft_bump_thick
FEATURE [Sketcher::SketchObject] Sketch025
  FullyConstrained = true
  MapMode = 5
  Placement = pos=(-1.46e-14,40,2.52e-14) rot=(-1,0,0;1.5708rad)
  Support = -> [Pad012]
  expr: Constraints[0] = Spreadsheet.serv_shaft_diam
  expr: Constraints[1] = Spreadsheet.serv_w / 2 + Spreadsheet.cb_thick
  expr: Constraints[2] = Spreadsheet.serv_w / 2
  sketch-geometry (1):
    g0: Circle CenterX=10 CenterY=-12 CenterZ=0 NormalX=0 NormalY=0 NormalZ=1 AngleXU=0 Radius=2.9
  constraints (3):
    c: Diameter(g0) = 5.8
    c: DistanceY(g0,g-1) = 12
    c: DistanceX(g-1,g0) = 10
FEATURE [Part::Part2DObjectPython] InvoluteGear  # Draft 2D object (typed FeaturePython)
  AddendumCoefficient = 1
  DedendumCoefficient = 1.25
  ExternalGear = true
  HighPrecision = true
  Modules = 0.23
  NumberOfTeeth = 25
  Placement = pos=(10,40,12) rot=(1,0,0;1.5708rad)
  PressureAngle = 20
  ProfileShiftCoefficient = 0
  RootFilletCoefficient = 0.38
  expr: .Placement.Base.x = Spreadsheet.serv_w / 2
  expr: .Placement.Base.y = Spreadsheet.serv_to_sec3 + Spreadsheet.serv_shaft_bump_thick
  expr: .Placement.Base.z = Spreadsheet.serv_w / 2 + Spreadsheet.cb_thick
FEATURE [PartDesign::Pad] Pad013
  BaseFeature = -> Pad012
  Direction = (0,-1,2e-16)
  Length = 5
  Length2 = 10
  Placement = pos=(0,0,0) rot=(1,0,0;1.5708rad)
  Profile = -> InvoluteGear
  ReferenceAxis = -> InvoluteGear [N_Axis]
  Reversed = true
  Type = 0
  expr: Length = Spreadsheet.serv_shaft_len
FEATURE [Sketcher::SketchObject] Sketch026
  FullyConstrained = true
  MapMode = 5
  Placement = pos=(0,45,0) rot=(-1,0,0;1.5708rad)
  Support = -> [Pad013]
  expr: Constraints[0] = Spreadsheet.serv_w / 2
  expr: Constraints[1] = Spreadsheet.serv_shaft_hole_diam
  expr: Constraints[2] = Spreadsheet.cb_thick + Spreadsheet.serv_w / 2
  sketch-geometry (1):
    g0: Circle CenterX=10 CenterY=-12 CenterZ=0 NormalX=0 NormalY=0 NormalZ=1 AngleXU=0 Radius=1.3
  constraints (3):
    c: DistanceX(g-1,g0) = 10
    c: Diameter(g0) = 2.6
    c: DistanceY(g0,g-1) = 12
FEATURE [PartDesign::Pocket] Pocket004
  BaseFeature = -> Pad013
  Direction = (0,-1,-2e-16)
  Length = 5
  Length2 = 5
  Placement = pos=(0,0,0) rot=(1,0,0;1.5708rad)
  Profile = -> Sketch026
  ReferenceAxis = -> Sketch026 [N_Axis]
  Type = 0
  expr: Length = Spreadsheet.serv_shaft_len
FEATURE [PartDesign::Body] Body004  label="servo_body"
  Group = -> [Sketch020,Pad008,Sketch021,Sketch022,Pad009,Pad010,Sketch023,Pad011,Fillet,Sketch024,Pad012,Sketch025,InvoluteGear,Pad013,Sketch026,Pocket004]
  Origin = -> Origin009
  Tip = -> Pocket004
FEATURE [PartDesign::Pad] Pad014
  Direction = (0,-1,-2e-16)
  Length = 51.3
  Length2 = 10
  Placement = pos=(0,0,0) rot=(1,0,0;1.5708rad)
  Profile = -> Sketch018
  ReferenceAxis = -> Sketch018 [N_Axis]
  Reversed = true
  Type = 0
  expr: Length = Spreadsheet.mh_len
FEATURE [Sketcher::SketchObject] Sketch027
  FullyConstrained = true
  MapMode = 5
  Placement = pos=(0,0,0) rot=(1,0,0;1.5708rad)
  Support = -> [XZ_Plane007]
  expr: Constraints[2] = Spreadsheet.dcm_diam + Spreadsheet.mh_thick * 2
  expr: Constraints[3] = Spreadsheet.mh_dcm_dist_from_origin + Spreadsheet.mh_thick
  expr: Constraints[4] = Spreadsheet.mh_thick + Spreadsheet.cb_thick
  expr: Constraints[5] = Spreadsheet.dcm_diam / 2
  expr: Constraints[6] = Spreadsheet.dcm_diam / 2
  sketch-geometry (4):
    g0: LineSegment StartX=18 StartY=4 StartZ=0 EndX=18 EndY=20.25 EndZ=0
    g1: LineSegment StartX=54.5 StartY=4 StartZ=0 EndX=54.5 EndY=20.25 EndZ=0
    g2: LineSegment StartX=18 StartY=4 StartZ=0 EndX=54.5 EndY=4 EndZ=0
    g3: ArcOfCircle CenterX=36.25 CenterY=20.25 CenterZ=0 NormalX=0 NormalY=0 NormalZ=1 AngleXU=0 Radius=18.25 StartAngle=1e-16 EndAngle=3.14159
  constraints (13):
    c: Vertical(g0)
    c: Vertical(g1)
    c: DistanceX(g0,g1) = 36.5
    c: DistanceX(g-1,g1) = 54.5
    c: DistanceY(g-1,g0) = 4
    c: DistanceY(g0,g0) = 16.25
    c: DistanceY(g1,g1) = 16.25
    c: Coincident(g2,g0)
    c: Coincident(g2,g1)
    c: Horizontal(g2)
    c: Coincident(g3,g0)
    c: Coincident(g3,g1)
    c: DistanceY(g3,g0) = 0
FEATURE [Sketcher::SketchObject] Sketch028
  FullyConstrained = true
  MapMode = 5
  Placement = pos=(0,-9e-16,4) rot=(0,0,1;3.14159rad)
  Support = -> [Pad014]
  expr: Constraints[10] = Spreadsheet.mh_dcm_dist_from_origin + Spreadsheet.mh_thick + Spreadsheet.mh_tolerance
  expr: Constraints[11] = Spreadsheet.mh_thick * 2 + Spreadsheet.mh_dcm_hole_diam
  expr: Constraints[9] = Spreadsheet.mh_len
  sketch-geometry (4):
    g0: LineSegment StartX=-55.5 StartY=0 StartZ=0 EndX=-18 EndY=0 EndZ=0
    g1: LineSegment StartX=-18 StartY=0 StartZ=0 EndX=-18 EndY=-51.3 EndZ=0
    g2: LineSegment StartX=-18 StartY=-51.3 StartZ=0 EndX=-55.5 EndY=-51.3 EndZ=0
    g3: LineSegment StartX=-55.5 StartY=-51.3 StartZ=0 EndX=-55.5 EndY=0 EndZ=0
  constraints (12):
    c: Coincident(g0,g1)
    c: Coincident(g1,g2)
    c: Coincident(g2,g3)
    c: Coincident(g3,g0)
    c: Horizontal(g0)
    c: Horizontal(g2)
    c: Vertical(g1)
    c: Vertical(g3)
    c: PointOnObject(g0,g-1)
    c: DistanceY(g2,g0) = 51.3
    c: DistanceX(g0,g-1) = 55.5
    c: DistanceX(g2,g1) = 37.5
FEATURE [PartDesign::Pad] Pad015
  BaseFeature = -> Pad014
  Direction = (0,-2e-16,1)
  Length = 35.5
  Length2 = 10
  Placement = pos=(0,0,0) rot=(1,0,0;1.5708rad)
  Profile = -> Sketch028
  ReferenceAxis = -> Sketch028 [N_Axis]
  Type = 0
  expr: Length = Spreadsheet.mh_dcm_hole_diam + Spreadsheet.mh_thick
FEATURE [Sketcher::SketchObject] Sketch031
  FullyConstrained = true
  MapMode = 5
  Placement = pos=(0,0,0) rot=(1,0,0;1.5708rad)
  Support = -> [Pad015]
  expr: Constraints[0] = Spreadsheet.mh_thick + Spreadsheet.cb_thick + Spreadsheet.dcm_outer_shaft_bump_outer_ring_to_bottom - Spreadsheet.dcm_outer_shaft_bump_outer_ring_diam / 2
  expr: Constraints[1] = Spreadsheet.mh_dcm_dist_from_origin - Spreadsheet.dcm_diam / 2
  expr: Constraints[2] = Spreadsheet.dcm_outer_shaft_bump_outer_ring_diam
  sketch-geometry (1):
    g0: Circle CenterX=36.25 CenterY=14.3 CenterZ=0 NormalX=0 NormalY=0 NormalZ=1 AngleXU=0 Radius=7.1
  constraints (3):
    c: DistanceY(g-1,g0) = 14.3
    c: DistanceX(g-1,g0) = 36.25
    c: Diameter(g0) = 14.2
FEATURE [PartDesign::Fillet] Fillet001
  Base = -> Pad015 [Edge12,Edge26]
  BaseFeature = -> Pad015
  Placement = pos=(0,0,0) rot=(1,0,0;1.5708rad)
  Radius = 18.4167
  SupportTransform = false
  UseAllEdges = false
  expr: Radius = Spreadsheet.mh_dcm_hole_diam / 2 + Spreadsheet.mh_thick / 1.2
FEATURE [PartDesign::Pocket] Pocket005
  BaseFeature = -> Fillet001
  Direction = (0,1,2e-16)
  Length = 2
  Length2 = 5
  Placement = pos=(0,0,0) rot=(1,0,0;1.5708rad)
  Profile = -> Sketch031
  ReferenceAxis = -> Sketch031 [N_Axis]
  Type = 0
  expr: Length = Spreadsheet.mh_thick
FEATURE [Sketcher::SketchObject] Sketch032
  FullyConstrained = true
  MapMode = 5
  Placement = pos=(0,51.3,1.14e-14) rot=(-1,0,0;1.5708rad)
  Support = -> [Pocket005]
  expr: Constraints[0] = Spreadsheet.mh_dcm_hole_diam
  expr: Constraints[1] = Spreadsheet.mh_dcm_dist_from_origin - Spreadsheet.dcm_diam / 2 + Spreadsheet.mh_tolerance / 2
  expr: Constraints[2] = Spreadsheet.mh_thick + Spreadsheet.cb_thick + Spreadsheet.mh_dcm_hole_diam / 2
  sketch-geometry (1):
    g0: Circle CenterX=36.75 CenterY=-20.75 CenterZ=0 NormalX=0 NormalY=0 NormalZ=1 AngleXU=0 Radius=16.75
  constraints (3):
    c: Diameter(g0) = 33.5
    c: DistanceX(g-1,g0) = 36.75
    c: DistanceY(g0,g-1) = 20.75
FEATURE [PartDesign::Pocket] Pocket006
  BaseFeature = -> Pocket005
  Direction = (0,-1,-2e-16)
  Length = 49.3
  Length2 = 5
  Placement = pos=(0,0,0) rot=(1,0,0;1.5708rad)
  Profile = -> Sketch032
  ReferenceAxis = -> Sketch032 [N_Axis]
  Type = 0
  expr: Length = Spreadsheet.mh_len - Spreadsheet.mh_thick
FEATURE [PartDesign::Body] Body003  label="mount_dcm"
  Group = -> [Sketch018,Pad014,Sketch027,Sketch028,Pad015,Sketch031,Fillet001,Pocket005,Sketch032,Pocket006]
  Origin = -> Origin007
  Tip = -> Pocket006
FEATURE [App::Part] Part003  label="dcm mount"
  Group = -> [Body003]
  Origin = -> Origin006
  Placement = pos=(0,72,0) rot=(0,0,1;0rad)
  expr: .Placement.Base.y = Spreadsheet.cb_gear_hole_from_back + Spreadsheet.cb_gear_hole_offset + Spreadsheet.cb_gear_hole_h
FEATURE [Sketcher::SketchObject] Sketch033
  FullyConstrained = true
  MapMode = 5
  Placement = pos=(0,0,0) rot=(0.57735,0.57735,0.57735;2.0944rad)
  Support = -> [YZ_Plane011]
  expr: Constraints[25] = Spreadsheet.mh_servo_bottom_h
  expr: Constraints[26] = Spreadsheet.mh_servo_bottom_h
  expr: Constraints[28] = Spreadsheet.serv_h
  expr: Constraints[29] = Spreadsheet.mh_thick
  expr: Constraints[30] = Spreadsheet.mh_thick
  expr: Constraints[31] = Spreadsheet.mh_thick
  expr: Constraints[32] = Spreadsheet.mh_thick
  expr: Constraints[33] = Spreadsheet.mh_thick
  expr: Constraints[34] = Spreadsheet.serv_to_sec1 - Spreadsheet.serv_screw_thick + Spreadsheet.mh_tolerance
  sketch-geometry (12):
    g0: LineSegment StartX=0 StartY=0 StartZ=0 EndX=31.6 EndY=0 EndZ=0
    g1: LineSegment StartX=31.6 StartY=0 StartZ=0 EndX=31.6 EndY=60.7 EndZ=0
    g2: LineSegment StartX=31.6 StartY=60.7 StartZ=0 EndX=0 EndY=60.7 EndZ=0
    g3: LineSegment StartX=0 StartY=60.7 StartZ=0 EndX=0 EndY=50.7 EndZ=0
    g4: LineSegment StartX=0 StartY=0 StartZ=0 EndX=0 EndY=10 EndZ=0
    g5: LineSegment StartX=0 StartY=10 StartZ=0 EndX=2 EndY=10 EndZ=0
    g6: LineSegment StartX=2 StartY=10 StartZ=0 EndX=2 EndY=2 EndZ=0
    g7: LineSegment StartX=2 StartY=2 StartZ=0 EndX=29.6 EndY=2 EndZ=0
    g8: LineSegment StartX=29.6 StartY=2 StartZ=0 EndX=29.6 EndY=58.7 EndZ=0
    g9: LineSegment StartX=29.6 StartY=58.7 StartZ=0 EndX=2 EndY=58.7 EndZ=0
    g10: LineSegment StartX=2 StartY=58.7 StartZ=0 EndX=2 EndY=50.7 EndZ=0
    g11: LineSegment StartX=0 StartY=50.7 StartZ=0 EndX=2 EndY=50.7 EndZ=0
  constraints (35):
    c: Coincident(g0,g-1)
    c: PointOnObject(g0,g-1)
    c: Coincident(g1,g0)
    c: Vertical(g1)
    c: Coincident(g2,g1)
    c: PointOnObject(g2,g-2)
    c: Horizontal(g2)
    c: Coincident(g3,g2)
    c: PointOnObject(g3,g-2)
    c: Coincident(g4,g0)
    c: PointOnObject(g4,g-2)
    c: Coincident(g5,g4)
    c: Horizontal(g5)
    c: Vertical(g6)
    c: Coincident(g7,g6)
    c: Horizontal(g7)
    c: Coincident(g8,g7)
    c: Vertical(g8)
    c: Coincident(g9,g8)
    c: Horizontal(g9)
    c: Coincident(g10,g9)
    c: Vertical(g10)
    c: Coincident(g11,g3)
    c: Coincident(g11,g10)
    c: Horizontal(g11)
    c: DistanceY(g3,g2) = 10
    c: DistanceY(g0,g4) = 10
    c: Coincident(g5,g6)
    c: DistanceY(g4,g3) = 40.7
    c: DistanceX(g3,g10) = 2
    c: DistanceX(g4,g5) = 2
    c: DistanceY(g0,g6) = 2
    c: DistanceX(g7,g0) = 2
    c: DistanceY(g8,g1) = 2
    c: DistanceX(g3,g8) = 29.6
FEATURE [PartDesign::Pad] Pad016  label="main"
  Direction = (1,-2e-16,3e-16)
  Length = 28
  Length2 = 10
  Placement = pos=(0,0,0) rot=(1,1,1;2.0944rad)
  Profile = -> Sketch033
  ReferenceAxis = -> Sketch033 [N_Axis]
  Type = 0
  expr: Length = Spreadsheet.serv_w + Spreadsheet.mh_serv_extra_w - Spreadsheet.mh_thick
FEATURE [Part::Part2DObjectPython] InvoluteGear001  # Draft 2D object (typed FeaturePython)
  AddendumCoefficient = 1
  DedendumCoefficient = 1.25
  ExternalGear = true
  HighPrecision = true
  Modules = 0.23
  NumberOfTeeth = 25
  PressureAngle = 20
  ProfileShiftCoefficient = 0
  RootFilletCoefficient = 0.38
FEATURE [Part::Part2DObjectPython] InvoluteGear002  # Draft 2D object (typed FeaturePython)
  AddendumCoefficient = 1
  DedendumCoefficient = 1.25
  ExternalGear = true
  HighPrecision = true
  Modules = 0.8
  NumberOfTeeth = 25
  PressureAngle = 20
  ProfileShiftCoefficient = 0
  RootFilletCoefficient = 0.38
FEATURE [PartDesign::Pad] Pad017  label="main gear body"
  Direction = (0,0,1)
  Length = 7
  Length2 = 10
  Profile = -> InvoluteGear002
  ReferenceAxis = -> InvoluteGear002 [N_Axis]
  Reversed = true
  Type = 0
  expr: Length = Spreadsheet.serv_gear_thick
FEATURE [PartDesign::Pocket] Pocket007  label="gear shaped hole"
  BaseFeature = -> Pad017
  Direction = (0,0,-1)
  Length = 5
  Length2 = 5
  Profile = -> InvoluteGear001
  ReferenceAxis = -> InvoluteGear001 [N_Axis]
  Type = 0
  expr: Length = Spreadsheet.serv_shaft_len
FEATURE [Sketcher::SketchObject] Sketch035  label="gear screw hole sketch"
  FullyConstrained = true
  MapMode = 5
  Placement = pos=(0,0,-7) rot=(1,0,0;3.14159rad)
  Support = -> [Pocket007]
  expr: Constraints[1] = Spreadsheet.serv_gear_screw_diam
  sketch-geometry (1):
    g0: Circle CenterX=0 CenterY=0 CenterZ=0 NormalX=0 NormalY=0 NormalZ=1 AngleXU=0 Radius=1.4
  constraints (2):
    c: Coincident(g0,g-1)
    c: Diameter(g0) = 2.8
FEATURE [PartDesign::Pocket] Pocket008
  BaseFeature = -> Pocket007
  Direction = (0,0,1)
  Length = 2
  Length2 = 5
  Profile = -> Sketch035
  ReferenceAxis = -> Sketch035 [N_Axis]
  Type = 0
  expr: Length = Spreadsheet.serv_gear_thick - Spreadsheet.serv_shaft_len
FEATURE [PartDesign::Body] Body006  label="gear"
  Group = -> [InvoluteGear001,InvoluteGear002,Pad017,Pocket007,Sketch035,Pocket008]
  Origin = -> Origin012
  Placement = pos=(10,40.5,12) rot=(1,0,0;1.5708rad)
  Tip = -> Pocket008
  expr: .Placement.Base.x = Spreadsheet.serv_w / 2
  expr: .Placement.Base.y = Spreadsheet.serv_to_sec3 + Spreadsheet.serv_shaft_bump_thick + 0.5 mm
FEATURE [App::Part] Part004  label="servo"
  Group = -> [Body004,Body006]
  Origin = -> Origin008
  Placement = pos=(39.9,197,12) rot=(1,0,1;3.14159rad)
  expr: .Placement.Base.x = -2 mm + Spreadsheet.cb_width / 2 - 8.6 mm - Spreadsheet.serv_screw_hole_diam / 2
  expr: .Placement.Base.y = Spreadsheet.cb_height - (Spreadsheet.mh_thick + Spreadsheet.mh_tolerance - Spreadsheet.serv_screw_thick + Spreadsheet.serv_to_sec1) + Spreadsheet.serv_to_sec1 - Spreadsheet.serv_screw_thick
  expr: .Placement.Base.z = Spreadsheet.cb_thick + 10 mm
FEATURE [Sketcher::SketchObject] Sketch036  label="front axle holder sketch"
  AttachmentOffset = pos=(0,0,-140) rot=(0,0,1;0rad)
  FullyConstrained = true
  MapMode = 5
  Placement = pos=(0,140,3.11e-14) rot=(1,0,0;1.5708rad)
  Support = -> [XZ_Plane]
  expr: .AttachmentOffset.Base.z = -Spreadsheet.cb_height + Spreadsheet.cb_front_wheel_dist + Spreadsheet.cb_wheel_space_h / 2 + Spreadsheet.cb_axle_holder_h / 2
  expr: Constraints[10] = Spreadsheet.cb_thick
  expr: Constraints[11] = Spreadsheet.cb_axle_holder_len
  expr: Constraints[19] = Spreadsheet.cb_axle_holder_thick
  expr: Constraints[20] = Spreadsheet.cb_axle_holder_top_thick
  expr: Constraints[21] = Spreadsheet.cb_axle_holder_len
  expr: Constraints[22] = Spreadsheet.cb_thick
  expr: Constraints[23] = Spreadsheet.cb_wheel_space_w
  expr: Constraints[7] = Spreadsheet.cb_axle_holder_thick
  expr: Constraints[8] = Spreadsheet.cb_axle_holder_top_thick
  expr: Constraints[9] = Spreadsheet.cb_width - Spreadsheet.cb_wheel_space_w
  sketch-geometry (8):
    g0: LineSegment StartX=85 StartY=2 StartZ=0 EndX=95 EndY=2 EndZ=0
    g1: LineSegment StartX=85 StartY=2 StartZ=0 EndX=85 EndY=22 EndZ=0
    g2: LineSegment StartX=85 StartY=22 StartZ=0 EndX=95 EndY=22 EndZ=0
    g3: LineSegment StartX=95 StartY=22 StartZ=0 EndX=95 EndY=2 EndZ=0
    g4: LineSegment StartX=10 StartY=2 StartZ=0 EndX=20 EndY=2 EndZ=0
    g5: LineSegment StartX=20 StartY=2 StartZ=0 EndX=20 EndY=22 EndZ=0
    g6: LineSegment StartX=20 StartY=22 StartZ=0 EndX=10 EndY=22 EndZ=0
    g7: LineSegment StartX=10 StartY=22 StartZ=0 EndX=10 EndY=2 EndZ=0
  constraints (24):
    c: Horizontal(g0)
    c: Coincident(g1,g0)
    c: Coincident(g2,g1)
    c: Coincident(g3,g2)
    c: Coincident(g3,g0)
    c: Vertical(g3)
    c: Horizontal(g2)
    c: DistanceX(g0,g0) = 10
    c: DistanceX(g1,g2) = 10
    c: DistanceX(g-1,g0) = 95
    c: DistanceY(g-1,g0) = 2
    c: DistanceY(g0,g2) = 20
    c: Horizontal(g4)
    c: Coincident(g5,g4)
    c: Coincident(g6,g5)
    c: Horizontal(g6)
    c: Coincident(g7,g6)
    c: Coincident(g7,g4)
    c: Vertical(g7)
    c: DistanceX(g4,g4) = 10
    c: DistanceX(g6,g5) = 10
    c: DistanceY(g4,g6) = 20
    c: DistanceY(g-1,g4) = 2
    c: DistanceX(g-1,g4) = 10
FEATURE [PartDesign::Pad] Pad018
  BaseFeature = -> Pocket003
  Direction = (0,-1,-2e-16)
  Length = 10
  Length2 = 10
  Profile = -> Sketch036
  ReferenceAxis = -> Sketch036 [N_Axis]
  Reversed = true
  Type = 0
  expr: Length = Spreadsheet.cb_axle_holder_h
FEATURE [Sketcher::SketchObject] Sketch037  label="left front axle hole sketch"
  FullyConstrained = true
  MapMode = 5
  Placement = pos=(10,0,0) rot=(0.57735,-0.57735,-0.57735;2.0944rad)
  Support = -> [Pad018]
  expr: Constraints[0] = Spreadsheet.cb_height - Spreadsheet.cb_front_wheel_dist - Spreadsheet.cb_wheel_space_h / 2
  expr: Constraints[1] = Spreadsheet.cb_axle_holder_hole_height + Spreadsheet.cb_thick
  expr: Constraints[2] = Spreadsheet.cb_axle_hole_diameter
  sketch-geometry (1):
    g0: Circle CenterX=-145 CenterY=14 CenterZ=0 NormalX=0 NormalY=0 NormalZ=1 AngleXU=0 Radius=1.5
  constraints (3):
    c: DistanceX(g0,g-1) = 145
    c: DistanceY(g-1,g0) = 14
    c: Diameter(g0) = 3
FEATURE [Sketcher::SketchObject] Sketch038  label="right front axle hole sketch"
  FullyConstrained = true
  MapMode = 5
  Placement = pos=(95,0,0) rot=(0.57735,0.57735,0.57735;2.0944rad)
  Support = -> [Pad018]
  expr: Constraints[0] = Spreadsheet.cb_axle_hole_diameter
  expr: Constraints[1] = Spreadsheet.cb_height - Spreadsheet.cb_front_wheel_dist - Spreadsheet.cb_wheel_space_h / 2
  expr: Constraints[2] = Spreadsheet.cb_axle_holder_hole_height + Spreadsheet.cb_thick
  sketch-geometry (1):
    g0: Circle CenterX=145 CenterY=14 CenterZ=0 NormalX=0 NormalY=0 NormalZ=1 AngleXU=0 Radius=1.5
  constraints (3):
    c: Diameter(g0) = 3
    c: DistanceX(g-1,g0) = 145
    c: DistanceY(g-1,g0) = 14
FEATURE [PartDesign::Pocket] Pocket009  label="left front axle hole"
  BaseFeature = -> Pad018
  Direction = (1,0,0)
  Length = 2
  Length2 = 5
  Profile = -> Sketch037
  ReferenceAxis = -> Sketch037 [N_Axis]
  Type = 0
  expr: Length = Spreadsheet.cb_axle_holder_thick * 0.2
FEATURE [PartDesign::Pocket] Pocket010  label="right front axle hole"
  BaseFeature = -> Pocket009
  Direction = (-1,0,0)
  Length = 2
  Length2 = 5
  Profile = -> Sketch038
  ReferenceAxis = -> Sketch038 [N_Axis]
  Type = 0
  expr: Length = Spreadsheet.cb_axle_holder_thick * 0.2
FEATURE [Sketcher::SketchObject] Sketch039  label="rod sketch"
  FullyConstrained = true
  MapMode = 5
  Placement = pos=(0,0,0) rot=(0.57735,0.57735,0.57735;2.0944rad)
  Support = -> [YZ_Plane014]
  expr: Constraints[0] = Spreadsheet.rod_diam
  expr: Constraints[1] = Spreadsheet.cb_axle_holder_hole_height + Spreadsheet.cb_thick
  expr: Constraints[2] = Spreadsheet.cb_height - Spreadsheet.cb_front_wheel_dist - Spreadsheet.cb_wheel_space_h / 2
  sketch-geometry (1):
    g0: Circle CenterX=145 CenterY=14 CenterZ=0 NormalX=0 NormalY=0 NormalZ=1 AngleXU=0 Radius=1
  constraints (3):
    c: Diameter(g0) = 2
    c: DistanceY(g-1,g0) = 14
    c: DistanceX(g-1,g0) = 145
FEATURE [PartDesign::Pad] Pad019
  Direction = (1,-2e-16,3e-16)
  Length = 100.5
  Length2 = 10
  Placement = pos=(0,0,0) rot=(1,1,1;2.0944rad)
  Profile = -> Sketch039
  ReferenceAxis = -> Sketch039 [N_Axis]
  Type = 0
  expr: Length = Spreadsheet.rod_len
FEATURE [PartDesign::Body] Body007  label="rod body"
  Group = -> [Pad019,Sketch039]
  Origin = -> Origin014
  Tip = -> Pad019
FEATURE [App::Part] Part006  label="front rod"
  Group = -> [Body007]
  Origin = -> Origin013
  Placement = pos=(2.25,0,0) rot=(0,0,1;0rad)
  expr: .Placement.Base.x = Spreadsheet.cb_width / 2 - Spreadsheet.rod_len / 2
FEATURE [PartDesign::FeaturePython] InvoluteRack  # WARN: FeaturePython — macro-defined, semantics opaque (R4)
  AttacherType = Attacher::AttachEngine3D
  Placement = pos=(131,-57.475,11.5) rot=(0,1,0;-1.5708rad)
  add_endings = true
  beta = 0
  clearance = 0.25
  double_helix = false
  head = 0
  head_fillet = 0
  height = 5
  module = 0.8
  pressure_angle = 20
  properties_from_tool = false
  root_fillet = 0
  simplified = false
  teeth = 20
  thickness = 8.5
  transverse_pitch = 2.51327
  version = 1.2.0
  expr: .Placement.Base.y = -30.11 mm - Spreadsheet.cb_width / 2 + Spreadsheet.tm_rack_len / 2
  expr: module = 0.8 mm
  expr: thickness = 8.5 mm
FEATURE [Sketcher::SketchObject] Sketch040  label="rack arm right arm"
  FullyConstrained = true
  MapMode = 5
  Placement = pos=(131,-58.7316,11.5) rot=(-0.57735,0.57735,-0.57735;4.18879rad)
  Support = -> [InvoluteRack]
  expr: Constraints[11] = Spreadsheet.tm_rack_arm_odist
  expr: Constraints[8] = Spreadsheet.tm_rack_arm_thick
  expr: Constraints[9] = Spreadsheet.tm_rack_thick
  sketch-geometry (4):
    g0: LineSegment StartX=-3.25 StartY=5 StartZ=0 EndX=-1.25 EndY=5 EndZ=0
    g1: LineSegment StartX=-1.25 StartY=5 StartZ=0 EndX=-1.25 EndY=0 EndZ=0
    g2: LineSegment StartX=-1.25 StartY=0 StartZ=0 EndX=-3.25 EndY=0 EndZ=0
    g3: LineSegment StartX=-3.25 StartY=0 StartZ=0 EndX=-3.25 EndY=5 EndZ=0
  constraints (12):
    c: Coincident(g0,g1)
    c: Coincident(g1,g2)
    c: Coincident(g2,g3)
    c: Coincident(g3,g0)
    c: Horizontal(g0)
    c: Horizontal(g2)
    c: Vertical(g1)
    c: Vertical(g3)
    c: DistanceX(g0,g0) = 2
    c: DistanceY(g1,g0) = 5
    c: DistanceY(g-1,g1) = 0
    c: DistanceX(g1,g-1) = 1.25
FEATURE [Sketcher::SketchObject] Sketch041  label="rack arm left arm sketch"
  FullyConstrained = true
  MapMode = 5
  Placement = pos=(131,-8.46615,11.5) rot=(-0.57735,0.57735,0.57735;2.0944rad)
  Support = -> [InvoluteRack]
  expr: Constraints[11] = Spreadsheet.tm_rack_arm_odist
  expr: Constraints[8] = Spreadsheet.tm_rack_arm_thick
  expr: Constraints[9] = Spreadsheet.tm_rack_thick
  sketch-geometry (4):
    g0: LineSegment StartX=1.25 StartY=5 StartZ=0 EndX=3.25 EndY=5 EndZ=0
    g1: LineSegment StartX=3.25 StartY=5 StartZ=0 EndX=3.25 EndY=0 EndZ=0
    g2: LineSegment StartX=3.25 StartY=0 StartZ=0 EndX=1.25 EndY=0 EndZ=0
    g3: LineSegment StartX=1.25 StartY=0 StartZ=0 EndX=1.25 EndY=5 EndZ=0
  constraints (12):
    c: Coincident(g0,g1)
    c: Coincident(g1,g2)
    c: Coincident(g2,g3)
    c: Coincident(g3,g0)
    c: Horizontal(g0)
    c: Horizontal(g2)
    c: Vertical(g1)
    c: Vertical(g3)
    c: DistanceX(g0,g0) = 2
    c: DistanceY(g2,g0) = 5
    c: DistanceY(g-1,g2) = 0
    c: DistanceX(g-1,g2) = 1.25
FEATURE [PartDesign::Pad] Pad020  label="right arm"
  BaseFeature = -> InvoluteRack
  Direction = (1e-16,-1,1e-16)
  Length = 25.46
  Length2 = 10
  Placement = pos=(131,-57.475,11.5) rot=(0,1,0;-1.5708rad)
  Profile = -> Sketch040
  ReferenceAxis = -> Sketch040 [N_Axis]
  Type = 0
  expr: Length = Spreadsheet.tm_rack_arm_len
FEATURE [PartDesign::Pad] Pad021  label="left arm"
  BaseFeature = -> Pad020
  Direction = (-1e-16,1,-1e-16)
  Length = 25.46
  Length2 = 10
  Placement = pos=(131,-57.475,11.5) rot=(0,1,0;-1.5708rad)
  Profile = -> Sketch041
  ReferenceAxis = -> Sketch041 [N_Axis]
  Type = 0
  expr: Length = Spreadsheet.tm_rack_arm_len
FEATURE [PartDesign::Fillet] Fillet002
  Base = -> Pad021 [Edge274,Edge184,Edge278,Edge191]
  BaseFeature = -> Pad021
  Placement = pos=(131,-57.475,11.5) rot=(0,1,0;-1.5708rad)
  Radius = 2.38095
  SupportTransform = false
  UseAllEdges = false
  expr: Radius = Spreadsheet.tm_rack_thick / 2.1
FEATURE [Sketcher::SketchObject] Sketch042  label="rack arm right hole"
  FullyConstrained = true
  MapMode = 5
  Placement = pos=(131,-57.475,10.25) rot=(0,0,1;1.5708rad)
  Support = -> [Fillet002]
  expr: Constraints[0] = Spreadsheet.tm_screw_diam
  expr: Constraints[1] = Spreadsheet.tm_rack_arm_len + 1.25 mm - Spreadsheet.tm_screw_diam / 2 - (Spreadsheet.tm_rack_thick - Spreadsheet.tm_screw_diam) / 2
  expr: Constraints[2] = Spreadsheet.tm_rack_thick / 2
  sketch-geometry (1):
    g0: Circle CenterX=-24.21 CenterY=2.5 CenterZ=0 NormalX=0 NormalY=0 NormalZ=1 AngleXU=0 Radius=1.25
  constraints (3):
    c: Diameter(g0) = 2.5
    c: DistanceX(g0,g-1) = 24.21
    c: DistanceY(g-1,g0) = 2.5
FEATURE [Sketcher::SketchObject] Sketch043  label="rack amr left hole"
  FullyConstrained = true
  MapMode = 5
  Placement = pos=(131,-57.475,10.25) rot=(0,0,1;1.5708rad)
  Support = -> [Fillet002]
  expr: Constraints[0] = Spreadsheet.tm_rack_len - 2.5 mm + Spreadsheet.tm_rack_arm_len + 1.25 mm - Spreadsheet.tm_screw_diam / 2 - (Spreadsheet.tm_rack_thick - Spreadsheet.tm_screw_diam) / 2
  expr: Constraints[1] = Spreadsheet.tm_rack_thick / 2
  expr: Constraints[2] = Spreadsheet.tm_screw_diam
  sketch-geometry (1):
    g0: Circle CenterX=71.98 CenterY=2.5 CenterZ=0 NormalX=0 NormalY=0 NormalZ=1 AngleXU=0 Radius=1.25
  constraints (3):
    c: DistanceX(g-1,g0) = 71.98
    c: DistanceY(g-1,g0) = 2.5
    c: Diameter(g0) = 2.5
FEATURE [PartDesign::Pocket] Pocket011  label="right rack hole"
  BaseFeature = -> Fillet002
  Direction = (9e-16,-1e-16,-1)
  Length = 2
  Length2 = 5
  Placement = pos=(131,-57.475,11.5) rot=(0,1,0;-1.5708rad)
  Profile = -> Sketch042
  ReferenceAxis = -> Sketch042 [N_Axis]
  Type = 0
  expr: Length = Spreadsheet.tm_rack_arm_thick
FEATURE [PartDesign::Pocket] Pocket012  label="left rack hole"
  BaseFeature = -> Pocket011
  Direction = (3e-16,-1e-16,-1)
  Length = 2
  Length2 = 5
  Placement = pos=(131,-57.475,11.5) rot=(0,1,0;-1.5708rad)
  Profile = -> Sketch043
  ReferenceAxis = -> Sketch043 [N_Axis]
  Type = 0
  expr: Length = Spreadsheet.tm_rack_arm_thick
FEATURE [PartDesign::Body] Body008  label="rack"
  Group = -> [InvoluteRack,Sketch040,Sketch041,Pad020,Pad021,Fillet002,Sketch042,Sketch043,Pocket011,Pocket012]
  Origin = -> Origin016
  Tip = -> Pocket012
FEATURE [Sketcher::SketchObject] Sketch044  label="left turning piece sketch"
  AttachmentOffset = pos=(-25.08,0,0) rot=(0,0,1;0rad)
  FullyConstrained = true
  MapMode = 5
  Placement = pos=(-25.08,0,0) rot=(1,0,0;1.5708rad)
  Support = -> [XZ_Plane017]
  expr: .AttachmentOffset.Base.x = -21.08 mm - Spreadsheet.rod_diam / 2 - Spreadsheet.tm_tp_wh / 2
  expr: .AttachmentOffset.Base.y = 0 mm
  expr: Constraints[10] = Spreadsheet.cb_height - Spreadsheet.cb_front_wheel_dist - Spreadsheet.cb_wheel_space_h / 2 + Spreadsheet.tm_tp_wh / 2
  expr: Constraints[11] = Spreadsheet.cb_thick + Spreadsheet.cb_axle_holder_hole_height - Spreadsheet.tm_tp_wh / 2
  expr: Constraints[8] = Spreadsheet.tm_tp_wh
  expr: Constraints[9] = Spreadsheet.tm_tp_wh
  sketch-geometry (4):
    g0: LineSegment StartX=142 StartY=17 StartZ=0 EndX=148 EndY=17 EndZ=0
    g1: LineSegment StartX=148 StartY=17 StartZ=0 EndX=148 EndY=11 EndZ=0
    g2: LineSegment StartX=148 StartY=11 StartZ=0 EndX=142 EndY=11 EndZ=0
    g3: LineSegment StartX=142 StartY=11 StartZ=0 EndX=142 EndY=17 EndZ=0
  constraints (12):
    c: Coincident(g0,g1)
    c: Coincident(g1,g2)
    c: Coincident(g2,g3)
    c: Coincident(g3,g0)
    c: Horizontal(g0)
    c: Horizontal(g2)
    c: Vertical(g1)
    c: Vertical(g3)
    c: DistanceX(g0,g0) = 6
    c: DistanceY(g2,g0) = 6
    c: DistanceX(g-1,g1) = 148
    c: DistanceY(g-1,g2) = 11
FEATURE [PartDesign::Pad] Pad022  label="turning piece left main "
  Direction = (0,-1,2e-16)
  Length = 7
  Length2 = 10
  Placement = pos=(0,0,0) rot=(1,0,0;1.5708rad)
  Profile = -> Sketch044
  ReferenceAxis = -> Sketch044 [N_Axis]
  Reversed = true
  Type = 0
  expr: Length = Spreadsheet.tm_tp_len
FEATURE [Sketcher::SketchObject] Sketch046
  FullyConstrained = true
  MapMode = 5
  Placement = pos=(0,0,0) rot=(1,0,0;1.5708rad)
  Support = -> [Pad022]
  expr: Constraints[0] = -25.08 mm + Spreadsheet.cb_height - Spreadsheet.cb_front_wheel_dist - Spreadsheet.cb_wheel_space_h / 2
  expr: Constraints[1] = Spreadsheet.tm_tp_tolerance + Spreadsheet.rod_diam
  expr: Constraints[2] = Spreadsheet.cb_thick + Spreadsheet.cb_axle_holder_hole_height
  sketch-geometry (1):
    g0: Circle CenterX=119.92 CenterY=14 CenterZ=0 NormalX=0 NormalY=0 NormalZ=1 AngleXU=0 Radius=1.25
  constraints (3):
    c: DistanceX(g-1,g0) = 119.92
    c: Diameter(g0) = 2.5
    c: DistanceY(g-1,g0) = 14
FEATURE [PartDesign::Pocket] Pocket013  label="turning piece left hole"
  BaseFeature = -> Pad022
  Direction = (0,1,-2e-16)
  Length = 5.6
  Length2 = 5
  Placement = pos=(0,0,0) rot=(1,0,0;1.5708rad)
  Profile = -> Sketch046
  ReferenceAxis = -> Sketch046 [N_Axis]
  Type = 0
  expr: Length = Spreadsheet.tm_tp_rod_in_len
FEATURE [Sketcher::SketchObject] Sketch047
  FullyConstrained = true
  MapMode = 5
  Placement = pos=(0,2.4e-15,11) rot=(1,0,0;3.14159rad)
  expr: Constraints[0] = -25.08 mm + Spreadsheet.cb_height - Spreadsheet.cb_front_wheel_dist - Spreadsheet.cb_wheel_space_h / 2
  expr: Constraints[1] = Spreadsheet.tm_tp_len / 2
  expr: Constraints[2] = Spreadsheet.tm_screw_diam
  sketch-geometry (1):
    g0: Circle CenterX=119.92 CenterY=-3.5 CenterZ=0 NormalX=0 NormalY=0 NormalZ=1 AngleXU=0 Radius=1.25
  constraints (3):
    c: DistanceX(g-1,g0) = 119.92
    c: DistanceY(g0,g-1) = 3.5
    c: Diameter(g0) = 2.5
FEATURE [PartDesign::Pad] Pad024  label="turning piece right rod"
  BaseFeature = -> Pocket013
  Direction = (0,-2e-16,-1)
  Length = 4.75
  Length2 = 10
  Placement = pos=(0,0,0) rot=(1,0,0;1.5708rad)
  Profile = -> Sketch047
  ReferenceAxis = -> Sketch047 [N_Axis]
  Type = 0
  expr: Length = Spreadsheet.tm_tp_spinny_rod_len
FEATURE [PartDesign::Body] Body009  label="turning piece left"
  Group = -> [Sketch044,Pad022,Sketch046,Pocket013,Sketch047,Pad024]
  Origin = -> Origin017
  Placement = pos=(0,11,0) rot=(0,0,1;0rad)
  Tip = -> Pad024
  expr: .Placement.Base.y = 16.6 mm - Spreadsheet.tm_tp_rod_in_len
FEATURE [Sketcher::SketchObject] Sketch048
  FullyConstrained = true
  MapMode = 5
  Support = -> [XY_Plane018]
  expr: Constraints[12] = Spreadsheet.tm_rack_thick
  expr: Constraints[13] = Spreadsheet.tm_rack_thick
  expr: Constraints[14] = Spreadsheet.tm_knuckle_len_racrod
  expr: Constraints[15] = Spreadsheet.tm_screw_diam / 2 + (Spreadsheet.tm_rack_thick - Spreadsheet.tm_screw_diam) / 2
  expr: Constraints[16] = Spreadsheet.tm_screw_diam / 2 + (Spreadsheet.tm_rack_thick - Spreadsheet.tm_screw_diam) / 2
  expr: Constraints[17] = Spreadsheet.tm_knuckle_len
  sketch-geometry (6):
    g0: LineSegment StartX=-2.5 StartY=-2.5 StartZ=0 EndX=11.08 EndY=-2.5 EndZ=0
    g1: LineSegment StartX=11.08 StartY=-2.5 StartZ=0 EndX=11.08 EndY=2.5 EndZ=0
    g2: LineSegment StartX=11.08 StartY=2.5 StartZ=0 EndX=2.5 EndY=2.5 EndZ=0
    g3: LineSegment StartX=2.5 StartY=2.5 StartZ=0 EndX=2.5 EndY=12.5 EndZ=0
    g4: LineSegment StartX=2.5 StartY=12.5 StartZ=0 EndX=-2.5 EndY=12.5 EndZ=0
    g5: LineSegment StartX=-2.5 StartY=12.5 StartZ=0 EndX=-2.5 EndY=-2.5 EndZ=0
  constraints (18):
    c: Horizontal(g0)
    c: Coincident(g1,g0)
    c: Vertical(g1)
    c: Coincident(g2,g1)
    c: Horizontal(g2)
    c: Coincident(g3,g2)
    c: Vertical(g3)
    c: Coincident(g4,g3)
    c: Horizontal(g4)
    c: Coincident(g5,g4)
    c: Coincident(g5,g0)
    c: Vertical(g5)
    c: DistanceY(g0,g2) = 5
    c: DistanceX(g0,g2) = 5
    c: DistanceX(g0,g0) = 13.58
    c: DistanceX(g0,g-1) = 2.5
    c: DistanceY(g0,g-1) = 2.5
    c: DistanceY(g2,g3) = 10
FEATURE [PartDesign::Pad] Pad025  label="main body"
  Direction = (0,0,1)
  Length = 2
  Length2 = 10
  Profile = -> Sketch048
  ReferenceAxis = -> Sketch048 [N_Axis]
  Type = 0
  expr: Length = Spreadsheet.tm_knuckle_thick
FEATURE [PartDesign::Fillet] Fillet003  label="curves on hinge"
  Base = -> Pad025 [Edge5,Edge2]
  BaseFeature = -> Pad025
  Radius = 2.38095
  SupportTransform = false
  UseAllEdges = false
  expr: Radius = Spreadsheet.tm_knuckle_w / 2.1
FEATURE [Sketcher::SketchObject] Sketch049
  FullyConstrained = true
  MapMode = 5
  Placement = pos=(0,0,0) rot=(1,0,0;3.14159rad)
  Support = -> [Fillet003]
  expr: Constraints[2] = Spreadsheet.tm_knuckle_len_racrod - Spreadsheet.tm_knuckle_w
  expr: Constraints[4] = Spreadsheet.tm_screw_diam
  sketch-geometry (2):
    g0: Circle CenterX=0 CenterY=0 CenterZ=0 NormalX=0 NormalY=0 NormalZ=1 AngleXU=0 Radius=1.25
    g1: Circle CenterX=8.58 CenterY=0 CenterZ=0 NormalX=0 NormalY=0 NormalZ=1 AngleXU=0 Radius=1.25
  constraints (5):
    c: Coincident(g0,g-1)
    c: PointOnObject(g1,g-1)
    c: DistanceX(g0,g1) = 8.58
    c: Equal(g1,g0)
    c: Diameter(g1) = 2.5
FEATURE [PartDesign::Pocket] Pocket014  label="holes"
  BaseFeature = -> Fillet003
  Direction = (0,0,1)
  Length = 2
  Length2 = 5
  Profile = -> Sketch049
  ReferenceAxis = -> Sketch049 [N_Axis]
  Type = 0
  expr: Length = Spreadsheet.tm_knuckle_thick
FEATURE [Sketcher::SketchObject] Sketch050  label="knuckle rod part"
  FullyConstrained = true
  MapMode = 5
  Placement = pos=(0,0,0) rot=(1,0,0;3.14159rad)
  Support = -> [Fillet003]
  expr: Constraints[10] = Spreadsheet.tm_rack_thick / 2
  expr: Constraints[11] = Spreadsheet.tm_knuckle_len + Spreadsheet.tm_rack_thick / 2
  expr: Constraints[8] = Spreadsheet.tm_rack_thick
  expr: Constraints[9] = Spreadsheet.tm_rack_thick / 2
  sketch-geometry (4):
    g0: LineSegment StartX=-2.5 StartY=-2.5 StartZ=0 EndX=2.5 EndY=-2.5 EndZ=0
    g1: LineSegment StartX=2.5 StartY=-2.5 StartZ=0 EndX=2.5 EndY=-12.5 EndZ=0
    g2: LineSegment StartX=2.5 StartY=-12.5 StartZ=0 EndX=-2.5 EndY=-12.5 EndZ=0
    g3: LineSegment StartX=-2.5 StartY=-12.5 StartZ=0 EndX=-2.5 EndY=-2.5 EndZ=0
  constraints (12):
    c: Coincident(g0,g1)
    c: Coincident(g1,g2)
    c: Coincident(g2,g3)
    c: Coincident(g3,g0)
    c: Horizontal(g0)
    c: Horizontal(g2)
    c: Vertical(g1)
    c: Vertical(g3)
    c: DistanceX(g0,g0) = 5
    c: DistanceY(g0,g-1) = 2.5
    c: DistanceX(g2,g-1) = 2.5
    c: DistanceY(g2,g-1) = 12.5
FEATURE [PartDesign::Pad] Pad026  label="second bump"
  BaseFeature = -> Pocket014
  Direction = (0,0,-1)
  Length = 3
  Length2 = 10
  Profile = -> Sketch050
  ReferenceAxis = -> Sketch050 [N_Axis]
  Type = 0
  expr: Length = Spreadsheet.tm_knuckle_thick_bump
FEATURE [Sketcher::SketchObject] Sketch051
  FullyConstrained = true
  MapMode = 5
  Placement = pos=(0,12.5,0) rot=(0,0.707107,0.707107;3.14159rad)
  Support = -> [Pad026]
  expr: Constraints[1] = (Spreadsheet.tm_knuckle_thick_bump - Spreadsheet.tm_knuckle_thick) / 2
  expr: Constraints[2] = Spreadsheet.rod_diam
  sketch-geometry (1):
    g0: Circle CenterX=0 CenterY=-0.5 CenterZ=0 NormalX=0 NormalY=0 NormalZ=1 AngleXU=0 Radius=1
  constraints (3):
    c: PointOnObject(g0,g-2)
    c: DistanceY(g0,g-1) = 0.5
    c: Diameter(g0) = 2
FEATURE [PartDesign::Pad] Pad027  label="knuckle rod"
  BaseFeature = -> Pad026
  Direction = (0,1,-2e-16)
  Length = 5
  Length2 = 10
  Profile = -> Sketch051
  ReferenceAxis = -> Sketch051 [N_Axis]
  Type = 0
  expr: Length = Spreadsheet.tm_knuckle_rod_len
FEATURE [PartDesign::Body] Body010  label="knuckle left"
  Group = -> [Sketch048,Pad025,Fillet003,Sketch049,Pocket014,Sketch050,Pad026,Sketch051,Pad027]
  Origin = -> Origin018
  Placement = pos=(119.92,14.5,6.25) rot=(0,0,1;0rad)
  Tip = -> Pad027
  expr: .Placement.Base.x = -25.08 mm + Spreadsheet.cb_height - Spreadsheet.cb_front_wheel_dist - Spreadsheet.cb_wheel_space_h / 2
  expr: .Placement.Base.y = 14.5 mm
  expr: .Placement.Base.z = Spreadsheet.tm_rack_arm_base_height
FEATURE [Sketcher::SketchObject] Sketch052
  FullyConstrained = true
  MapMode = 5
  Placement = pos=(0,0,0) rot=(1,0,0;1.5708rad)
  Support = -> [XZ_Plane019]
  expr: Constraints[10] = Spreadsheet.cb_height - Spreadsheet.tm_offset_back - Spreadsheet.cb_front_wheel_dist - Spreadsheet.cb_wheel_space_h / 2 - Spreadsheet.tm_tp_wh / 2
  expr: Constraints[11] = Spreadsheet.cb_thick + Spreadsheet.cb_axle_holder_hole_height / 2 + Spreadsheet.tm_tp_wh / 2
  expr: Constraints[8] = Spreadsheet.tm_tp_wh
  expr: Constraints[9] = Spreadsheet.tm_tp_wh
  sketch-geometry (4):
    g0: LineSegment StartX=116.92 StartY=17 StartZ=0 EndX=122.92 EndY=17 EndZ=0
    g1: LineSegment StartX=122.92 StartY=17 StartZ=0 EndX=122.92 EndY=11 EndZ=0
    g2: LineSegment StartX=122.92 StartY=11 StartZ=0 EndX=116.92 EndY=11 EndZ=0
    g3: LineSegment StartX=116.92 StartY=11 StartZ=0 EndX=116.92 EndY=17 EndZ=0
  constraints (12):
    c: Coincident(g0,g1)
    c: Coincident(g1,g2)
    c: Coincident(g2,g3)
    c: Coincident(g3,g0)
    c: Horizontal(g0)
    c: Horizontal(g2)
    c: Vertical(g1)
    c: Vertical(g3)
    c: DistanceX(g0,g0) = 6
    c: DistanceY(g1,g0) = 6
    c: DistanceX(g-1,g2) = 116.92
    c: DistanceY(g-1,g2) = 11
FEATURE [PartDesign::Pad] Pad028  label="right knuckle body"
  Direction = (0,-1,2e-16)
  Length = 7
  Length2 = 10
  Placement = pos=(0,0,0) rot=(1,0,0;1.5708rad)
  Profile = -> Sketch052
  ReferenceAxis = -> Sketch052 [N_Axis]
  Type = 0
  expr: Length = Spreadsheet.tm_tp_len
FEATURE [Sketcher::SketchObject] Sketch053  label="rod circle sketch"
  FullyConstrained = true
  MapMode = 5
  Placement = pos=(0,2.4e-15,11) rot=(1,0,0;3.14159rad)
  Support = -> [Pad028]
  expr: Constraints[0] = Spreadsheet.tm_screw_diam
  expr: Constraints[1] = Spreadsheet.tm_tp_len / 2
  expr: Constraints[2] = Spreadsheet.cb_height - Spreadsheet.tm_offset_back - Spreadsheet.cb_front_wheel_dist - Spreadsheet.cb_wheel_space_h / 2
  sketch-geometry (1):
    g0: Circle CenterX=119.92 CenterY=3.5 CenterZ=0 NormalX=0 NormalY=0 NormalZ=1 AngleXU=0 Radius=1.25
  constraints (3):
    c: Diameter(g0) = 2.5
    c: DistanceY(g-1,g0) = 3.5
    c: DistanceX(g-1,g0) = 119.92
FEATURE [PartDesign::Pad] Pad029  label="right knuckle wheel rod"
  BaseFeature = -> Pad028
  Direction = (0,-2e-16,-1)
  Length = 4.75
  Length2 = 10
  Placement = pos=(0,0,0) rot=(1,0,0;1.5708rad)
  Profile = -> Sketch053
  ReferenceAxis = -> Sketch053 [N_Axis]
  Type = 0
  expr: Length = Spreadsheet.tm_tp_spinny_rod_len
FEATURE [PartDesign::Body] Body011  label="turning piece right"
  Group = -> [Sketch052,Pad028,Sketch053,Pad029]
  Origin = -> Origin019
  Placement = pos=(0,-78.2,0) rot=(0,0,1;0rad)
  Tip = -> Pad029
  expr: .Placement.Base.y = -Spreadsheet.cb_width + Spreadsheet.tm_tp_offset_origin + Spreadsheet.tm_tp_offset_side
FEATURE [Sketcher::SketchObject] Sketch054  label="knuckle right main sketch"
  FullyConstrained = true
  MapMode = 5
  Support = -> [XY_Plane020]
  expr: Constraints[12] = Spreadsheet.tm_knuckle_w
  expr: Constraints[13] = Spreadsheet.tm_tp_offset_side - Spreadsheet.tm_tp_len / 2 - Spreadsheet.tm_knuckle_w / 2
  expr: Constraints[14] = Spreadsheet.tm_knuckle_w
  expr: Constraints[15] = Spreadsheet.tm_knuckle_w / 2
  expr: Constraints[16] = Spreadsheet.tm_knuckle_len_racrod
  expr: Constraints[17] = Spreadsheet.tm_knuckle_len
  sketch-geometry (6):
    g0: LineSegment StartX=11.08 StartY=6.9 StartZ=0 EndX=11.08 EndY=1.9 EndZ=0
    g1: LineSegment StartX=11.08 StartY=1.9 StartZ=0 EndX=2.5 EndY=1.9 EndZ=0
    g2: LineSegment StartX=11.08 StartY=6.9 StartZ=0 EndX=-2.5 EndY=6.9 EndZ=0
    g3: LineSegment StartX=2.5 StartY=1.9 StartZ=0 EndX=2.5 EndY=-8.1 EndZ=0
    g4: LineSegment StartX=2.5 StartY=-8.1 StartZ=0 EndX=-2.5 EndY=-8.1 EndZ=0
    g5: LineSegment StartX=-2.5 StartY=6.9 StartZ=0 EndX=-2.5 EndY=-8.1 EndZ=0
  constraints (18):
    c: Vertical(g0)
    c: Coincident(g1,g0)
    c: Horizontal(g1)
    c: Coincident(g2,g0)
    c: Horizontal(g2)
    c: Coincident(g3,g1)
    c: Vertical(g3)
    c: Coincident(g4,g3)
    c: Horizontal(g4)
    c: Coincident(g5,g2)
    c: Coincident(g5,g4)
    c: Vertical(g5)
    c: DistanceY(g1,g2) = 5
    c: DistanceY(g-1,g0) = 1.9
    c: DistanceX(g2,g1) = 5
    c: DistanceX(g-1,g1) = 2.5
    c: DistanceX(g2,g0) = 13.58
    c: DistanceY(g3,g1) = 10
FEATURE [PartDesign::Pad] Pad030  label="knuckle right main "
  Direction = (0,0,1)
  Length = 2
  Length2 = 10
  Profile = -> Sketch054
  ReferenceAxis = -> Sketch054 [N_Axis]
  Reversed = true
  Type = 0
  expr: Length = Spreadsheet.tm_knuckle_thick
FEATURE [Sketcher::SketchObject] Sketch055  label="knuckle right hole sketch"
  FullyConstrained = true
  MapMode = 5
  Placement = pos=(0,0,-2) rot=(1,0,0;3.14159rad)
  Support = -> [Pad030]
  expr: Constraints[1] = Spreadsheet.tm_screw_diam
  expr: Constraints[2] = Spreadsheet.tm_tp_offset_side - Spreadsheet.tm_tp_len / 2
  expr: Constraints[3] = 0 mm
  expr: Constraints[4] = Spreadsheet.tm_knuckle_len_racrod - Spreadsheet.tm_knuckle_w
  expr: Constraints[5] = Spreadsheet.tm_screw_diam
  sketch-geometry (2):
    g0: Circle CenterX=0 CenterY=-4.4 CenterZ=0 NormalX=0 NormalY=0 NormalZ=1 AngleXU=0 Radius=1.25
    g1: Circle CenterX=8.58 CenterY=-4.4 CenterZ=0 NormalX=0 NormalY=0 NormalZ=1 AngleXU=0 Radius=1.25
  constraints (6):
    c: PointOnObject(g0,g-2)
    c: Diameter(g0) = 2.5
    c: DistanceY(g0,g-1) = 4.4
    c: DistanceY(g1,g0) = 0
    c: DistanceX(g0,g1) = 8.58
    c: Diameter(g1) = 2.5
FEATURE [PartDesign::Pocket] Pocket015  label="knuckle right hole"
  BaseFeature = -> Pad030
  Direction = (0,0,1)
  Length = 2
  Length2 = 5
  Profile = -> Sketch055
  ReferenceAxis = -> Sketch055 [N_Axis]
  Type = 0
  expr: Length = Spreadsheet.tm_knuckle_thick
FEATURE [PartDesign::Fillet] Fillet004
  Base = -> Pocket015 [Edge2,Edge1]
  BaseFeature = -> Pocket015
  Radius = 2.38095
  SupportTransform = false
  UseAllEdges = false
  expr: Radius = Spreadsheet.tm_knuckle_w / 2.1
FEATURE [Sketcher::SketchObject] Sketch056  label="knuckle right bump sketch"
  FullyConstrained = true
  MapMode = 5
  Placement = pos=(0,0,-2) rot=(1,0,0;3.14159rad)
  Support = -> [Fillet004]
  expr: Constraints[10] = Spreadsheet.tm_knuckle_w
  expr: Constraints[11] = Spreadsheet.tm_knuckle_len
  expr: Constraints[8] = Spreadsheet.tm_tp_offset_side - Spreadsheet.tm_tp_len / 2 - Spreadsheet.tm_knuckle_w / 2
  expr: Constraints[9] = Spreadsheet.tm_knuckle_w / 2
  sketch-geometry (4):
    g0: LineSegment StartX=-2.5 StartY=8.1 StartZ=0 EndX=2.5 EndY=8.1 EndZ=0
    g1: LineSegment StartX=2.5 StartY=8.1 StartZ=0 EndX=2.5 EndY=-1.9 EndZ=0
    g2: LineSegment StartX=2.5 StartY=-1.9 StartZ=0 EndX=-2.5 EndY=-1.9 EndZ=0
    g3: LineSegment StartX=-2.5 StartY=-1.9 StartZ=0 EndX=-2.5 EndY=8.1 EndZ=0
  constraints (12):
    c: Coincident(g0,g1)
    c: Coincident(g1,g2)
    c: Coincident(g2,g3)
    c: Coincident(g3,g0)
    c: Horizontal(g0)
    c: Horizontal(g2)
    c: Vertical(g1)
    c: Vertical(g3)
    c: DistanceY(g2,g-1) = 1.9
    c: DistanceX(g2,g-1) = 2.5
    c: DistanceX(g2,g1) = 5
    c: DistanceY(g1,g0) = 10
FEATURE [PartDesign::Pad] Pad031  label="knuckle right bump"
  BaseFeature = -> Fillet004
  Direction = (0,0,-1)
  Length = 3
  Length2 = 10
  Profile = -> Sketch056
  ReferenceAxis = -> Sketch056 [N_Axis]
  Type = 0
  expr: Length = Spreadsheet.tm_knuckle_thick_bump
FEATURE [Sketcher::SketchObject] Sketch057
  FullyConstrained = true
  MapMode = 5
  Placement = pos=(0,-8.1,0) rot=(1,0,0;1.5708rad)
  Support = -> [Pad031]
  expr: Constraints[1] = Spreadsheet.rod_diam
  expr: Constraints[2] = (Spreadsheet.tm_knuckle_thick + Spreadsheet.tm_knuckle_thick_bump) / 2
  sketch-geometry (1):
    g0: Circle CenterX=0 CenterY=-2.5 CenterZ=0 NormalX=0 NormalY=0 NormalZ=1 AngleXU=0 Radius=1
  constraints (3):
    c: PointOnObject(g0,g-2)
    c: Diameter(g0) = 2
    c: DistanceY(g0,g-1) = 2.5
FEATURE [PartDesign::Pad] Pad032
  BaseFeature = -> Pad031
  Direction = (0,-1,2e-16)
  Length = 5
  Length2 = 10
  Profile = -> Sketch057
  ReferenceAxis = -> Sketch057 [N_Axis]
  Type = 0
  expr: Length = Spreadsheet.tm_knuckle_rod_len
FEATURE [PartDesign::Body] Body012  label="knuckle right"
  Group = -> [Sketch054,Pad030,Sketch055,Pocket015,Fillet004,Sketch056,Pad031,Sketch057,Pad032]
  Origin = -> Origin020
  Placement = pos=(119.92,-86.1,8.25) rot=(0,0,1;0rad)
  Tip = -> Pad032
  expr: .Placement.Base.x = -Spreadsheet.tm_offset_back + Spreadsheet.cb_height - Spreadsheet.cb_front_wheel_dist - Spreadsheet.cb_wheel_space_h / 2
  expr: .Placement.Base.y = Spreadsheet.tm_tp_offset_origin - Spreadsheet.cb_width
  expr: .Placement.Base.z = Spreadsheet.cb_thick + Spreadsheet.tm_rack_arm_top_dist - Spreadsheet.tm_rack_arm_thick
FEATURE [App::Part] Part007  label="turning mechanism"
  Group = -> [Body008,Body009,Body010,Body011,Body012]
  Origin = -> Origin015
  Placement = pos=(18.9025,25.0797,-1.8e-15) rot=(0,0,1;1.5708rad)
FEATURE [Sketcher::SketchObject] Sketch058
  FullyConstrained = true
  MapMode = 5
  Placement = pos=(0,0,0) rot=(0.57735,0.57735,0.57735;2.0944rad)
  Support = -> [YZ_Plane022]
  expr: Constraints[0] = Spreadsheet.cb_back_wheel_dist + Spreadsheet.cb_wheel_space_h / 2
  expr: Constraints[1] = Spreadsheet.cb_thick + Spreadsheet.cb_axle_holder_hole_height
  expr: Constraints[2] = Spreadsheet.wheel_back_diam
  sketch-geometry (1):
    g0: Circle CenterX=50 CenterY=14 CenterZ=0 NormalX=0 NormalY=0 NormalZ=1 AngleXU=0 Radius=30
  constraints (3):
    c: DistanceX(g-1,g0) = 50
    c: DistanceY(g-1,g0) = 14
    c: Diameter(g0) = 60
FEATURE [Sketcher::SketchObject] Sketch059
  FullyConstrained = true
  MapMode = 5
  Placement = pos=(0,0,2) rot=(0,0,1;0rad)
  Support = -> [Pocket010]
  expr: Constraints[11] = Spreadsheet.cb_height
  expr: Constraints[12] = Spreadsheet.cb_rack_front_dist - Spreadsheet.cb_rh_gap_tolerance / 2
  expr: Constraints[13] = Spreadsheet.cb_width / 2 - Spreadsheet.cb_rh_len / 2
  expr: Constraints[22] = Spreadsheet.cb_rh_thick
  expr: Constraints[23] = Spreadsheet.cb_rh_len
  expr: Constraints[24] = Spreadsheet.cb_width / 2 - Spreadsheet.cb_rh_len / 2
  expr: Constraints[25] = Spreadsheet.cb_rack_front_dist + Spreadsheet.cb_rh_gap_tolerance / 2 + Spreadsheet.tm_rack_thick
  expr: Constraints[8] = Spreadsheet.cb_rh_thick
  expr: Constraints[9] = Spreadsheet.cb_rh_len
  sketch-geometry (9):
    g0: LineSegment StartX=82.5 StartY=158.48 StartZ=0 EndX=22.5 EndY=158.48 EndZ=0
    g1: LineSegment StartX=22.5 StartY=158.48 StartZ=0 EndX=22.5 EndY=156.48 EndZ=0
    g2: LineSegment StartX=22.5 StartY=156.48 StartZ=0 EndX=82.5 EndY=156.48 EndZ=0
    g3: LineSegment StartX=82.5 StartY=156.48 StartZ=0 EndX=82.5 EndY=158.48 EndZ=0
    g4: GeomPoint X=0 Y=200 Z=0
    g5: LineSegment StartX=82.5 StartY=150.68 StartZ=0 EndX=22.5 EndY=150.68 EndZ=0
    g6: LineSegment StartX=22.5 StartY=150.68 StartZ=0 EndX=22.5 EndY=148.68 EndZ=0
    g7: LineSegment StartX=22.5 StartY=148.68 StartZ=0 EndX=82.5 EndY=148.68 EndZ=0
    g8: LineSegment StartX=82.5 StartY=148.68 StartZ=0 EndX=82.5 EndY=150.68 EndZ=0
  constraints (26):
    c: Coincident(g0,g1)
    c: Coincident(g1,g2)
    c: Coincident(g2,g3)
    c: Coincident(g3,g0)
    c: Horizontal(g0)
    c: Horizontal(g2)
    c: Vertical(g1)
    c: Vertical(g3)
    c: DistanceY(g2,g0) = 2
    c: DistanceX(g1,g2) = 60
    c: PointOnObject(g4,g-2)
    c: DistanceY(g-1,g4) = 200
    c: DistanceY(g1,g4) = 43.52
    c: DistanceX(g-1,g0) = 22.5
    c: Coincident(g5,g6)
    c: Coincident(g6,g7)
    c: Coincident(g7,g8)
    c: Coincident(g8,g5)
    c: Horizontal(g5)
    c: Horizontal(g7)
    c: Vertical(g6)
    c: Vertical(g8)
    c: DistanceY(g7,g5) = 2
    c: DistanceX(g6,g7) = 60
    c: DistanceX(g-1,g6) = 22.5
    c: DistanceY(g5,g4) = 49.32
FEATURE [PartDesign::Pad] Pad033
  BaseFeature = -> Pocket010
  Direction = (0,0,1)
  Length = 4.25
  Length2 = 10
  Profile = -> Sketch059
  ReferenceAxis = -> Sketch059 [N_Axis]
  Type = 0
  expr: Length = Spreadsheet.cb_rh_h
FEATURE [Sketcher::SketchObject] Sketch060
  FullyConstrained = true
  MapMode = 5
  Placement = pos=(28,-1.24e-14,9.3e-15) rot=(0.57735,0.57735,0.57735;2.0944rad)
  Support = -> [Pad016]
  expr: Constraints[10] = Spreadsheet.serv_h + 2 * Spreadsheet.mh_servo_bottom_h
  expr: Constraints[9] = Spreadsheet.serv_to_sec1 - Spreadsheet.serv_screw_thick + Spreadsheet.mh_tolerance + Spreadsheet.mh_thick
  sketch-geometry (4):
    g0: LineSegment StartX=0 StartY=0 StartZ=0 EndX=31.6 EndY=0 EndZ=0
    g1: LineSegment StartX=31.6 StartY=0 StartZ=0 EndX=31.6 EndY=60.7 EndZ=0
    g2: LineSegment StartX=31.6 StartY=60.7 StartZ=0 EndX=0 EndY=60.7 EndZ=0
    g3: LineSegment StartX=0 StartY=60.7 StartZ=0 EndX=0 EndY=0 EndZ=0
  constraints (11):
    c: Coincident(g0,g1)
    c: Coincident(g1,g2)
    c: Coincident(g2,g3)
    c: Coincident(g3,g0)
    c: Horizontal(g0)
    c: Horizontal(g2)
    c: Vertical(g1)
    c: Vertical(g3)
    c: Coincident(g0,g-1)
    c: DistanceX(g0,g0) = 31.6
    c: DistanceY(g0,g2) = 60.7
FEATURE [PartDesign::Pad] Pad034
  BaseFeature = -> Pad016
  Direction = (1,-4e-16,4e-16)
  Length = 2
  Length2 = 10
  Placement = pos=(0,0,0) rot=(1,1,1;2.0944rad)
  Profile = -> Sketch060
  ReferenceAxis = -> Sketch060 [N_Axis]
  Type = 0
  expr: Length = Spreadsheet.mh_thick
FEATURE [PartDesign::Body] Body005  label="mount"
  Group = -> [Sketch033,Pad016,Sketch060,Pad034]
  Origin = -> Origin011
  Tip = -> Pad034
FEATURE [App::Part] Part005  label="servo mount"
  Group = -> [Body005]
  Origin = -> Origin010
  Placement = pos=(31.9,168.4,32) rot=(0,1,0;1.5708rad)
  expr: .Placement.Base.x = (Spreadsheet.mh_servo_bottom_h * 2 + Spreadsheet.serv_h) / 2 + 1.55 mm
  expr: .Placement.Base.y = Spreadsheet.cb_height - (Spreadsheet.serv_to_sec1 - Spreadsheet.serv_screw_thick + Spreadsheet.mh_tolerance) - Spreadsheet.mh_thick
  expr: .Placement.Base.z = Spreadsheet.cb_thick + 30 mm
FEATURE [PartDesign::Pad] Pad035  label="wheel  bl main pad"
  Direction = (1,0,0)
  Length = 7.25
  Length2 = 10
  Placement = pos=(0,0,0) rot=(1,1,1;2.0944rad)
  Profile = -> Sketch058
  ReferenceAxis = -> Sketch058 [N_Axis]
  Type = 0
  expr: Length = Spreadsheet.wheel_back_thick + Spreadsheet.wheel_back_edge_thick
FEATURE [Sketcher::SketchObject] Sketch063  label="axle holder extra piece front"
  FullyConstrained = true
  MapMode = 5
  Placement = pos=(0,140,0) rot=(1,0,0;1.5708rad)
  Support = -> [Pad033]
  expr: Constraints[10] = Spreadsheet.cb_wheel_space_w
  expr: Constraints[18] = Spreadsheet.cb_axle_holder_top_thick + Spreadsheet.cb_axle_holder_in_len
  expr: Constraints[19] = Spreadsheet.cb_axle_holder_len
  expr: Constraints[20] = Spreadsheet.cb_axle_holder_thick + Spreadsheet.cb_axle_holder_in_len
  expr: Constraints[21] = Spreadsheet.cb_thick
  expr: Constraints[22] = Spreadsheet.cb_width - Spreadsheet.cb_wheel_space_w
  expr: Constraints[6] = Spreadsheet.cb_axle_holder_top_thick + Spreadsheet.cb_axle_holder_in_len
  expr: Constraints[7] = Spreadsheet.cb_axle_holder_top_thick + Spreadsheet.cb_axle_holder_in_len
  expr: Constraints[8] = Spreadsheet.cb_axle_holder_len
  expr: Constraints[9] = Spreadsheet.cb_thick
  sketch-geometry (8):
    g0: LineSegment StartX=10 StartY=22 StartZ=0 EndX=10 EndY=2 EndZ=0
    g1: LineSegment StartX=10 StartY=2 StartZ=0 EndX=30 EndY=2 EndZ=0
    g2: LineSegment StartX=30 StartY=2 StartZ=0 EndX=30 EndY=22 EndZ=0
    g3: LineSegment StartX=30 StartY=22 StartZ=0 EndX=10 EndY=22 EndZ=0
    g4: LineSegment StartX=75 StartY=22 StartZ=0 EndX=95 EndY=22 EndZ=0
    g5: LineSegment StartX=95 StartY=22 StartZ=0 EndX=95 EndY=2 EndZ=0
    g6: LineSegment StartX=95 StartY=2 StartZ=0 EndX=75 EndY=2 EndZ=0
    g7: LineSegment StartX=75 StartY=2 StartZ=0 EndX=75 EndY=22 EndZ=0
  constraints (24):
    c: Vertical(g0)
    c: Coincident(g1,g0)
    c: Horizontal(g1)
    c: Coincident(g2,g1)
    c: Coincident(g3,g2)
    c: Coincident(g3,g0)
    c: DistanceX(g0,g2) = 20
    c: DistanceX(g0,g1) = 20
    c: DistanceY(g0,g0) = 20
    c: DistanceY(g-1,g0) = 2
    c: DistanceX(g-1,g0) = 10
    c: Horizontal(g3)
    c: Horizontal(g4)
    c: Coincident(g5,g4)
    c: Vertical(g5)
    c: Coincident(g6,g5)
    c: Coincident(g7,g6)
    c: Coincident(g7,g4)
    c: DistanceX(g4,g4) = 20
    c: DistanceY(g5,g4) = 20
    c: DistanceX(g6,g5) = 20
    c: DistanceY(g-1,g5) = 2
    c: DistanceX(g-1,g5) = 95
    c: Horizontal(g6)
FEATURE [PartDesign::Pad] Pad037  label="front axle holder extra"
  BaseFeature = -> Pad033
  Direction = (0,-1,2e-16)
  Length = 10
  Length2 = 10
  Profile = -> Sketch063
  ReferenceAxis = -> Sketch063 [N_Axis]
  Type = 0
  expr: Length = Spreadsheet.cb_axle_holder_h_extra
FEATURE [Sketcher::SketchObject] Sketch065  label="axle holder extra piece back"
  FullyConstrained = true
  MapMode = 5
  Placement = pos=(0,45,1.6e-14) rot=(1,0,0;1.5708rad)
  Support = -> [Pad037]
  expr: Constraints[10] = Spreadsheet.cb_wheel_space_w
  expr: Constraints[18] = Spreadsheet.cb_axle_holder_len
  expr: Constraints[19] = Spreadsheet.cb_axle_holder_top_thick
  expr: Constraints[20] = Spreadsheet.cb_axle_holder_thick
  expr: Constraints[21] = Spreadsheet.cb_thick
  expr: Constraints[22] = Spreadsheet.cb_width - Spreadsheet.cb_wheel_space_w
  expr: Constraints[6] = Spreadsheet.cb_axle_holder_top_thick
  expr: Constraints[7] = Spreadsheet.cb_axle_holder_thick
  expr: Constraints[8] = Spreadsheet.cb_axle_holder_len
  expr: Constraints[9] = Spreadsheet.cb_thick
  sketch-geometry (8):
    g0: LineSegment StartX=10 StartY=22 StartZ=0 EndX=20 EndY=22 EndZ=0
    g1: LineSegment StartX=20 StartY=22 StartZ=0 EndX=20 EndY=2 EndZ=0
    g2: LineSegment StartX=20 StartY=2 StartZ=0 EndX=10 EndY=2 EndZ=0
    g3: LineSegment StartX=10 StartY=2 StartZ=0 EndX=10 EndY=22 EndZ=0
    g4: LineSegment StartX=85 StartY=22 StartZ=0 EndX=95 EndY=22 EndZ=0
    g5: LineSegment StartX=95 StartY=22 StartZ=0 EndX=95 EndY=2 EndZ=0
    g6: LineSegment StartX=95 StartY=2 StartZ=0 EndX=85 EndY=2 EndZ=0
    g7: LineSegment StartX=85 StartY=2 StartZ=0 EndX=85 EndY=22 EndZ=0
  constraints (24):
    c: Horizontal(g0)
    c: Coincident(g1,g0)
    c: Coincident(g2,g1)
    c: Horizontal(g2)
    c: Coincident(g3,g2)
    c: Coincident(g3,g0)
    c: DistanceX(g0,g0) = 10
    c: DistanceX(g2,g1) = 10
    c: DistanceY(g1,g0) = 20
    c: DistanceY(g-1,g2) = 2
    c: DistanceX(g-1,g2) = 10
    c: Horizontal(g4)
    c: Coincident(g5,g4)
    c: Vertical(g5)
    c: Coincident(g6,g5)
    c: Horizontal(g6)
    c: Coincident(g7,g6)
    c: Coincident(g7,g4)
    c: DistanceY(g5,g4) = 20
    c: DistanceX(g4,g4) = 10
    c: DistanceX(g6,g5) = 10
    c: DistanceY(g-1,g5) = 2
    c: DistanceX(g-1,g5) = 95
    c: Vertical(g3)
FEATURE [PartDesign::Pad] Pad038  label="back axle holder extra"
  BaseFeature = -> Pad037
  Direction = (0,-1,-2e-16)
  Length = 22
  Length2 = 10
  Profile = -> Sketch065
  ReferenceAxis = -> Sketch065 [N_Axis]
  Type = 0
  expr: Length = Spreadsheet.cb_axle_holder_h_extra_back
FEATURE [Sketcher::SketchObject] Sketch066  label="back axle extra inward piece"
  FullyConstrained = true
  MapMode = 5
  Placement = pos=(0,23,8.2e-15) rot=(1,0,0;1.5708rad)
  Support = -> [Pad038]
  expr: Constraints[16] = Spreadsheet.cb_axle_holder_thick + Spreadsheet.cb_axle_holder_in_len
  expr: Constraints[17] = Spreadsheet.cb_axle_holder_len
  expr: Constraints[18] = Spreadsheet.cb_wheel_space_w
  expr: Constraints[19] = Spreadsheet.cb_thick
  expr: Constraints[20] = Spreadsheet.cb_width - Spreadsheet.cb_wheel_space_w
  expr: Constraints[21] = Spreadsheet.cb_thick
  expr: Constraints[22] = Spreadsheet.cb_axle_holder_len
  expr: Constraints[23] = Spreadsheet.cb_axle_holder_thick + Spreadsheet.cb_axle_holder_in_len
  sketch-geometry (8):
    g0: LineSegment StartX=10 StartY=22 StartZ=0 EndX=30 EndY=22 EndZ=0
    g1: LineSegment StartX=30 StartY=22 StartZ=0 EndX=30 EndY=2 EndZ=0
    g2: LineSegment StartX=30 StartY=2 StartZ=0 EndX=10 EndY=2 EndZ=0
    g3: LineSegment StartX=10 StartY=2 StartZ=0 EndX=10 EndY=22 EndZ=0
    g4: LineSegment StartX=95 StartY=22 StartZ=0 EndX=75 EndY=22 EndZ=0
    g5: LineSegment StartX=75 StartY=22 StartZ=0 EndX=75 EndY=2 EndZ=0
    g6: LineSegment StartX=75 StartY=2 StartZ=0 EndX=95 EndY=2 EndZ=0
    g7: LineSegment StartX=95 StartY=2 StartZ=0 EndX=95 EndY=22 EndZ=0
  constraints (24):
    c: Coincident(g0,g1)
    c: Coincident(g1,g2)
    c: Coincident(g2,g3)
    c: Coincident(g3,g0)
    c: Horizontal(g0)
    c: Horizontal(g2)
    c: Vertical(g1)
    c: Vertical(g3)
    c: Coincident(g4,g5)
    c: Coincident(g5,g6)
    c: Coincident(g6,g7)
    c: Coincident(g7,g4)
    c: Horizontal(g4)
    c: Horizontal(g6)
    c: Vertical(g5)
    c: Vertical(g7)
    c: DistanceX(g0,g0) = 20
    c: DistanceY(g2,g0) = 20
    c: DistanceX(g-1,g2) = 10
    c: DistanceY(g-1,g2) = 2
    c: DistanceX(g-1,g6) = 95
    c: DistanceY(g-1,g6) = 2
    c: DistanceY(g6,g4) = 20
    c: DistanceX(g4,g4) = 20
FEATURE [PartDesign::Pad] Pad039
  BaseFeature = -> Pad038
  Direction = (0,-1,-2e-16)
  Length = 10
  Length2 = 10
  Profile = -> Sketch066
  ReferenceAxis = -> Sketch066 [N_Axis]
  Type = 0
  expr: Length = Spreadsheet.cb_axle_holder_thick
FEATURE [PartDesign::Body] Body
  Group = -> [Sketch,Pad,Sketch007,Pocket001,Sketch015,Sketch014,Sketch016,Pad006,Pocket002,Pocket003,Sketch036,Pad018,Sketch037,Sketch038,Pocket009,Pocket010,Sketch059,Pad033,Sketch063,Pad037,Sketch065,Pad038,Sketch066,Pad039]
  Origin = -> Origin
  Tip = -> Pad039
FEATURE [App::Part] Part  label="car base"
  Group = -> [Body]
  Origin = -> Origin001
FEATURE [Sketcher::SketchObject] Sketch067  label="wheel edge sketch"
  FullyConstrained = true
  MapMode = 5
  Placement = pos=(7.25,-3.2e-15,2.4e-15) rot=(0.57735,0.57735,0.57735;2.0944rad)
  Support = -> [Pad035]
  expr: Constraints[0] = Spreadsheet.cb_back_wheel_dist + Spreadsheet.cb_wheel_space_h / 2
  expr: Constraints[1] = Spreadsheet.cb_thick + Spreadsheet.cb_axle_holder_hole_height
  expr: Constraints[2] = Spreadsheet.wheel_back_diam - Spreadsheet.wheel_back_edge_thick * 2
  sketch-geometry (1):
    g0: Circle CenterX=50 CenterY=14 CenterZ=0 NormalX=0 NormalY=0 NormalZ=1 AngleXU=0 Radius=25
  constraints (3):
    c: DistanceX(g-1,g0) = 50
    c: DistanceY(g-1,g0) = 14
    c: Diameter(g0) = 50
FEATURE [PartDesign::Pocket] Pocket016  label="wheel bl edge pocket"
  BaseFeature = -> Pad035
  Direction = (-1,4e-16,-4e-16)
  Length = 5
  Length2 = 5
  Placement = pos=(0,0,0) rot=(1,1,1;2.0944rad)
  Profile = -> Sketch067
  ReferenceAxis = -> Sketch067 [N_Axis]
  Type = 0
  expr: Length = Spreadsheet.wheel_back_edge_thick
FEATURE [Sketcher::SketchObject] Sketch068
  FullyConstrained = true
  MapMode = 5
  Placement = pos=(2.25,-1.5e-15,1.3e-15) rot=(0.57735,0.57735,0.57735;2.0944rad)
  Support = -> [Pocket016]
  expr: Constraints[0] = Spreadsheet.cb_back_wheel_dist + Spreadsheet.cb_wheel_space_h / 2
  expr: Constraints[1] = Spreadsheet.cb_thick + Spreadsheet.cb_axle_holder_hole_height
  expr: Constraints[2] = Spreadsheet.wheel_hole_wall_thick * 2 + Spreadsheet.wheel_hole_diam
  sketch-geometry (1):
    g0: Circle CenterX=50 CenterY=14 CenterZ=0 NormalX=0 NormalY=0 NormalZ=1 AngleXU=0 Radius=3
  constraints (3):
    c: DistanceX(g-1,g0) = 50
    c: DistanceY(g-1,g0) = 14
    c: Diameter(g0) = 6
FEATURE [PartDesign::Pad] Pad040  label=" wheel bl holder pad"
  BaseFeature = -> Pocket016
  Direction = (1,-7e-16,7e-16)
  Length = 4
  Length2 = 10
  Placement = pos=(0,0,0) rot=(1,1,1;2.0944rad)
  Profile = -> Sketch068
  ReferenceAxis = -> Sketch068 [N_Axis]
  Type = 0
  expr: Length = Spreadsheet.wheel_holder_len
FEATURE [Sketcher::SketchObject] Sketch069  label="wheel bl hole sketch"
  FullyConstrained = true
  MapMode = 5
  Placement = pos=(6.25,-5.1e-15,5e-15) rot=(0.57735,0.57735,0.57735;2.0944rad)
  Support = -> [Pad040]
  expr: Constraints[0] = Spreadsheet.cb_thick + Spreadsheet.cb_axle_holder_hole_height
  expr: Constraints[1] = Spreadsheet.cb_back_wheel_dist + Spreadsheet.cb_wheel_space_h / 2
  expr: Constraints[2] = Spreadsheet.wheel_hole_diam
  sketch-geometry (1):
    g0: Circle CenterX=50 CenterY=14 CenterZ=0 NormalX=0 NormalY=0 NormalZ=1 AngleXU=0 Radius=1
  constraints (3):
    c: DistanceY(g-1,g0) = 14
    c: DistanceX(g-1,g0) = 50
    c: Diameter(g0) = 2
FEATURE [PartDesign::Pocket] Pocket017
  BaseFeature = -> Pad040
  Direction = (-1,9e-16,-9e-16)
  Length = 4
  Length2 = 5
  Placement = pos=(0,0,0) rot=(1,1,1;2.0944rad)
  Profile = -> Sketch069
  ReferenceAxis = -> Sketch069 [N_Axis]
  Type = 0
  expr: Length = Spreadsheet.wheel_holder_len
FEATURE [PartDesign::Body] Body013  label="wheel back left"
  Group = -> [Sketch058,Pad035,Sketch067,Pocket016,Sketch068,Pad040,Sketch069,Pocket017]
  Origin = -> Origin022
  Tip = -> Pocket017
FEATURE [Sketcher::SketchObject] Sketch070
  FullyConstrained = true
  MapMode = 5
  Placement = pos=(0,0,0) rot=(0.57735,0.57735,0.57735;2.0944rad)
  Support = -> [YZ_Plane023]
  expr: Constraints[0] = 4.75 mm + Spreadsheet.rod_diam / 2
  expr: Constraints[1] = Spreadsheet.cb_height - Spreadsheet.cb_front_wheel_dist - Spreadsheet.cb_wheel_space_h / 2
  expr: Constraints[2] = Spreadsheet.wheel_front_diam
  sketch-geometry (1):
    g0: Circle CenterX=145 CenterY=5.75 CenterZ=0 NormalX=0 NormalY=0 NormalZ=1 AngleXU=0 Radius=21.75
  constraints (3):
    c: DistanceY(g-1,g0) = 5.75
    c: DistanceX(g-1,g0) = 145
    c: Diameter(g0) = 43.5
FEATURE [PartDesign::Pad] Pad041
  Direction = (1,0,0)
  Length = 2.25
  Length2 = 10
  Placement = pos=(0,0,0) rot=(1,1,1;2.0944rad)
  Profile = -> Sketch070
  ReferenceAxis = -> Sketch070 [N_Axis]
  Reversed = true
  Type = 0
  expr: Length = Spreadsheet.wheel_front_thick
FEATURE [PartDesign::Body] Body014  label="wheel front left"
  Group = -> [Sketch070,Pad041]
  Origin = -> Origin023
  Placement = pos=(-13.1,0,0) rot=(0,0,1;0rad)
  Tip = -> Pad041
  expr: .Placement.Base.x = -13.1 mm
FEATURE [App::Part] Part008  label="wheels"
  Group = -> [Body013,Body014]
  Origin = -> Origin021
